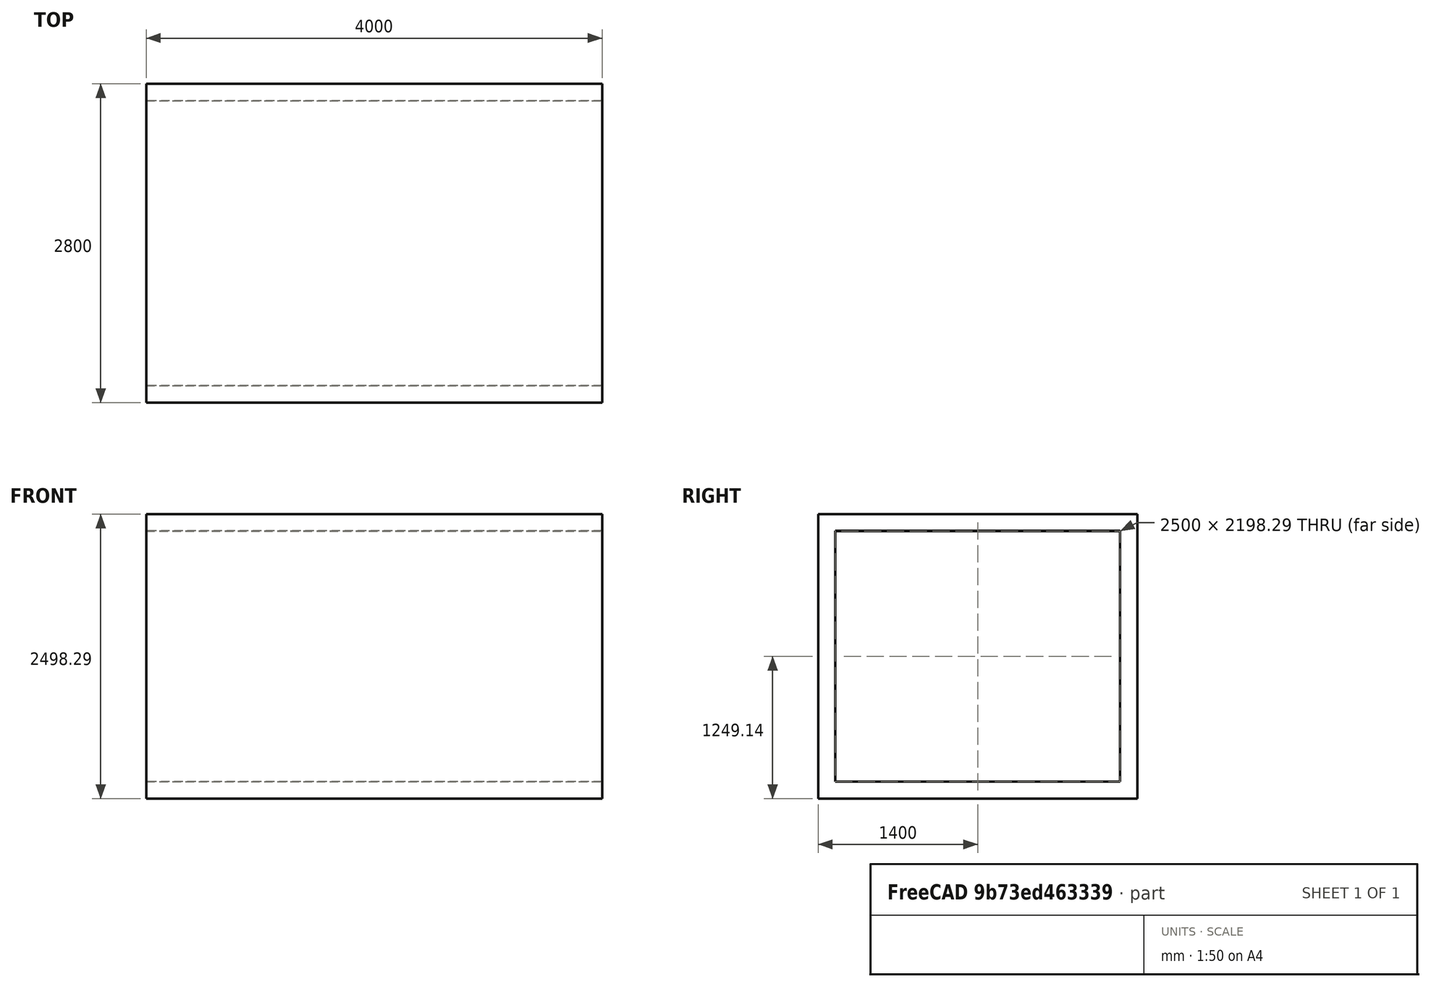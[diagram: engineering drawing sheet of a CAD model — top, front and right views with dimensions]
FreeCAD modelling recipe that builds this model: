
FCSTD DOCUMENT  (FreeCAD 0.17R10276 (Git))
Label: Model 01
License: CreativeCommons Attribution
LicenseURL: http://creativecommons.org/licenses/by/4.0/
objects: Part::Feature×203, Part::Part2DObjectPython×172, App::FeaturePython×39, Part::Mirroring×20, App::DocumentObjectGroup×15, App::Annotation×12, Part::Compound×9, Part::Extrusion×2, Part::FeaturePython×2, Part::Thickness×1, Sketcher::SketchObject×1
note: 410 computed .brp shape members not serialized (recipe doc carries the construction recipe); baked Part::Feature solids carry a one-line shape summary decoded from their .brp

FEATURE [Part::Part2DObjectPython] Rectangle  # Draft 2D object (typed FeaturePython)
  ChamferSize = 0
  Columns = 1
  FilletRadius = 0
  Height = 7500
  Length = 6000
  MakeFace = false
  MapMode = -1
  Placement = pos=(-92,-160,0) rot=(0,0,1;0rad)
  Rows = 1
FEATURE [App::FeaturePython] Dimension  # Draft dimension (typed FeaturePython)
  Diameter = false
  Dimline = (6612,4842,0)
  Direction = (0,0,0)
  Distance = 7500
  End = (5908,7340,0)
  LinkedGeometry = -> [Rectangle]
  Normal = (0,0,1)
  Start = (5908,-160,0)
  Support = -> Rectangle
FEATURE [App::FeaturePython] Dimension001  # Draft dimension (typed FeaturePython)
  Diameter = false
  Dimline = (3172,-852,0)
  Direction = (0,0,0)
  Distance = 6000
  End = (5908,-160,0)
  LinkedGeometry = -> [Rectangle]
  Normal = (0,0,1)
  Start = (-92,-160,0)
  Support = -> Rectangle
FEATURE [Part::Part2DObjectPython] Rectangle001  # Draft 2D object (typed FeaturePython)
  ChamferSize = 0
  Columns = 1
  FilletRadius = 0
  Height = 9000
  Length = 5000
  MakeFace = false
  MapMode = -1
  Placement = pos=(9194.87,-160,0) rot=(0,0,1;0rad)
  Rows = 1
FEATURE [App::FeaturePython] Dimension002  # Draft dimension (typed FeaturePython)
  Diameter = false
  Dimline = (15053,4856,0)
  Direction = (0,0,0)
  Distance = 9000
  End = (14194.9,8840,0)
  LinkedGeometry = -> [Rectangle001]
  Normal = (0,0,1)
  Start = (14194.9,-160,0)
  Support = -> Rectangle001
FEATURE [App::FeaturePython] Dimension003  # Draft dimension (typed FeaturePython)
  Diameter = false
  Dimline = (12458.9,-852,0)
  Direction = (0,0,0)
  Distance = 5000
  End = (14194.9,-160,0)
  LinkedGeometry = -> [Rectangle001]
  Normal = (0,0,1)
  Start = (9194.87,-160,0)
  Support = -> Rectangle001
FEATURE [Part::Part2DObjectPython] Rectangle002  # Draft 2D object (typed FeaturePython)
  ChamferSize = 0
  Columns = 1
  FilletRadius = 0
  Height = 11250
  Length = 4000
  MakeFace = false
  MapMode = -1
  Placement = pos=(17670.3,-160,0) rot=(0,0,1;0rad)
  Rows = 1
FEATURE [App::FeaturePython] Dimension004  # Draft dimension (typed FeaturePython)
  Diameter = false
  Dimline = (22786,4857,0)
  Direction = (0,0,0)
  Distance = 11250
  End = (21670.3,11090,0)
  LinkedGeometry = -> [Rectangle002]
  Normal = (0,0,1)
  Start = (21670.3,-160,0)
  Support = -> Rectangle002
FEATURE [App::FeaturePython] Dimension005  # Draft dimension (typed FeaturePython)
  Diameter = false
  Dimline = (20934.3,-852,0)
  Direction = (0,0,0)
  Distance = 4000
  End = (21670.3,-160,0)
  LinkedGeometry = -> [Rectangle002]
  Normal = (0,0,1)
  Start = (17670.3,-160,0)
  Support = -> Rectangle002
FEATURE [Part::Part2DObjectPython] Rectangle011  # Draft 2D object (typed FeaturePython)
  ChamferSize = 0
  Columns = 1
  FilletRadius = 0
  Height = 18
  Length = 900
  MakeFace = true
  Placement = pos=(3354.54,473.858,0) rot=(0.707107,0.707107,0;3.14159rad)
  Rows = 1
FEATURE [Part::Part2DObjectPython] Arc001  # Draft 2D object (typed FeaturePython)
  FirstAngle = -90
  LastAngle = 0
  MakeFace = true
  Placement = pos=(3372.54,473.858,0) rot=(0.707107,0.707107,0;3.14159rad)
  Radius = 900
FEATURE [Part::Part2DObjectPython] Rectangle012  # Draft 2D object (typed FeaturePython)
  ChamferSize = 0
  Columns = 1
  FilletRadius = 0
  Height = 18
  Length = 100
  MakeFace = true
  Placement = pos=(3390.54,373.858,0) rot=(0.707107,0.707107,0;3.14159rad)
  Rows = 1
FEATURE [Part::Part2DObjectPython] Rectangle013  # Draft 2D object (typed FeaturePython)
  ChamferSize = 0
  Columns = 1
  FilletRadius = 0
  Height = 18
  Length = 100
  MakeFace = true
  Placement = pos=(3372.54,373.858,0) rot=(0.707107,0.707107,0;3.14159rad)
  Rows = 1
FEATURE [Part::Part2DObjectPython] Rectangle014  # Draft 2D object (typed FeaturePython)
  ChamferSize = 0
  Columns = 1
  FilletRadius = 0
  Height = 18
  Length = 100
  MakeFace = true
  Placement = pos=(2436.54,373.858,0) rot=(0.707107,0.707107,0;3.14159rad)
  Rows = 1
FEATURE [Part::Part2DObjectPython] Rectangle015  # Draft 2D object (typed FeaturePython)
  ChamferSize = 0
  Columns = 1
  FilletRadius = 0
  Height = 18
  Length = 100
  MakeFace = true
  Placement = pos=(2454.54,373.858,0) rot=(0.707107,0.707107,0;3.14159rad)
  Rows = 1
FEATURE [Part::Compound] Compound001  label="Door-90cm"
  Links = -> [Rectangle015,Rectangle014,Rectangle011,Rectangle012,Arc001,Rectangle013]
  Placement = pos=(12065.1,-4816.3,0) rot=(0,0,1;0rad)
FEATURE [Part::Part2DObjectPython] Rectangle016  # Draft 2D object (typed FeaturePython)
  ChamferSize = 0
  Columns = 1
  FilletRadius = 0
  Height = 1450
  Length = 2250
  MakeFace = false
  Placement = pos=(19234,-3969.83,0) rot=(0.707107,0.707107,0;3.14159rad)
  Rows = 1
FEATURE [Part::Part2DObjectPython] Rectangle017  # Draft 2D object (typed FeaturePython)
  ChamferSize = 0
  Columns = 1
  FilletRadius = 0
  Height = 18
  Length = 800
  MakeFace = true
  Placement = pos=(4414.52,473.858,0) rot=(0.707107,0.707107,0;3.14159rad)
  Rows = 1
FEATURE [Part::Part2DObjectPython] Rectangle018  # Draft 2D object (typed FeaturePython)
  ChamferSize = 0
  Columns = 1
  FilletRadius = 0
  Height = 18
  Length = 100
  MakeFace = true
  Placement = pos=(4450.52,373.858,0) rot=(0.707107,0.707107,0;3.14159rad)
  Rows = 1
FEATURE [Part::Part2DObjectPython] Rectangle019  # Draft 2D object (typed FeaturePython)
  ChamferSize = 0
  Columns = 1
  FilletRadius = 0
  Height = 18
  Length = 100
  MakeFace = true
  Placement = pos=(4432.52,373.858,0) rot=(0.707107,0.707107,0;3.14159rad)
  Rows = 1
FEATURE [Part::Part2DObjectPython] Rectangle020  # Draft 2D object (typed FeaturePython)
  ChamferSize = 0
  Columns = 1
  FilletRadius = 0
  Height = 18
  Length = 100
  MakeFace = true
  Placement = pos=(3596.52,373.858,0) rot=(0.707107,0.707107,0;3.14159rad)
  Rows = 1
FEATURE [Part::Part2DObjectPython] Rectangle021  # Draft 2D object (typed FeaturePython)
  ChamferSize = 0
  Columns = 1
  FilletRadius = 0
  Height = 18
  Length = 100
  MakeFace = true
  Placement = pos=(3614.52,373.858,0) rot=(0.707107,0.707107,0;3.14159rad)
  Rows = 1
FEATURE [Part::Part2DObjectPython] Rectangle022  # Draft 2D object (typed FeaturePython)
  ChamferSize = 0
  Columns = 1
  FilletRadius = 0
  Height = 1655.27
  Length = 2455.27
  MakeFace = false
  Placement = pos=(19131.4,-4072.46,0) rot=(0.707107,0.707107,0;3.14159rad)
  Rows = 1
FEATURE [Part::Part2DObjectPython] Rectangle023  # Draft 2D object (typed FeaturePython)
  ChamferSize = 0
  Columns = 1
  FilletRadius = 0
  Height = 800
  Length = 800
  MakeFace = true
  Placement = pos=(21405.4,-1242.94,0) rot=(0.707107,0.707107,0;3.14159rad)
  Rows = 1
FEATURE [Part::Part2DObjectPython] Rectangle024  # Draft 2D object (typed FeaturePython)
  ChamferSize = 0
  Columns = 1
  FilletRadius = 0
  Height = 760
  Length = 760
  MakeFace = true
  Placement = pos=(21425.4,-1222.94,0) rot=(0.707107,0.707107,0;3.14159rad)
  Rows = 1
FEATURE [Part::Feature] Face
  Placement = pos=(15980.4,-1398.57,0) rot=(0,0,1;0rad)
  shape: bbox 800 x 800 x 2e-07 mm, 1 faces, 0 solids (baked)
FEATURE [Part::Part2DObjectPython] Rectangle025  # Draft 2D object (typed FeaturePython)
  ChamferSize = 0
  Columns = 1
  FilletRadius = 0
  Height = 760
  Length = 760
  MakeFace = true
  Placement = pos=(21425.4,-1222.94,0) rot=(0.707107,0.707107,0;3.14159rad)
  Rows = 1
FEATURE [Part::Part2DObjectPython] Line001  # Draft 2D object (typed FeaturePython)
  ChamferSize = 0
  Closed = false
  End = (21425.4,-1222.94,0)
  FilletRadius = 0
  Length = 1074.8
  MakeFace = true
  Placement = pos=(15980.4,-1398.57,0) rot=(0,0,1;0rad)
  Points = (2) [(6204.98,935.631,0),(5444.98,175.631,0)]
  Start = (22185.4,-462.938,0)
  Subdivisions = 0
FEATURE [Part::Part2DObjectPython] Line002  # Draft 2D object (typed FeaturePython)
  ChamferSize = 0
  Closed = false
  End = (22185.4,-1222.94,0)
  FilletRadius = 0
  Length = 1074.8
  MakeFace = true
  Placement = pos=(15980.4,-1398.57,0) rot=(0,0,1;0rad)
  Points = (2) [(5444.98,935.631,0),(6204.98,175.631,0)]
  Start = (21425.4,-462.938,0)
  Subdivisions = 0
FEATURE [Part::Part2DObjectPython] Block  label="Shower"  # Draft 2D object (typed FeaturePython)
  Components = -> [Line002,Line001,Rectangle025,Face]
  Placement = pos=(-1521.4,-1276.89,0) rot=(0,0,1;0rad)
FEATURE [Part::Part2DObjectPython] Rectangle026  # Draft 2D object (typed FeaturePython)
  ChamferSize = 0
  Columns = 1
  FilletRadius = 30
  Height = 370
  Length = 170
  MakeFace = true
  Placement = pos=(22375.3,-1817.54,0) rot=(0.707107,0.707107,0;3.14159rad)
  Rows = 1
FEATURE [Part::Part2DObjectPython] Circle  # Draft 2D object (typed FeaturePython)
  FirstAngle = 0
  LastAngle = 0
  MakeFace = true
  Placement = pos=(22560.3,-1732.54,0) rot=(0.707107,0.707107,0;3.14159rad)
  Radius = 10
  Support = -> [Rectangle026]
FEATURE [Part::Feature] Compound003  label="WC001"
  Placement = pos=(12977.9,-1470.8,0) rot=(0,0,1;0rad)
  shape: bbox 370 x 660 x 2e-07 mm, 2 faces, 0 solids (baked)
FEATURE [Part::Part2DObjectPython] Rectangle027  # Draft 2D object (typed FeaturePython)
  ChamferSize = 0
  Columns = 1
  FilletRadius = 50
  Height = 300
  Length = 500
  MakeFace = true
  Placement = pos=(21444.9,-2450.78,0) rot=(0.707107,0.707107,0;3.14159rad)
  Rows = 1
FEATURE [Part::Part2DObjectPython] Circle001  # Draft 2D object (typed FeaturePython)
  FirstAngle = 0
  LastAngle = 0
  MakeFace = true
  Placement = pos=(5532.19,-802.214,0) rot=(0,0,1;0rad)
  Radius = 12
FEATURE [Part::Feature] Face003
  shape: bbox 278.9 x 478.9 x 2e-07 mm, 1 faces, 0 solids (baked)
FEATURE [Part::Feature] Face004
  Placement = pos=(15980.4,-1398.57,0) rot=(0,0,1;0rad)
  shape: bbox 278.9 x 478.9 x 2e-07 mm, 1 faces, 0 solids (baked)
FEATURE [Part::Feature] Face005
  shape: bbox 300 x 500 x 2e-07 mm, 1 faces, 0 solids (baked)
FEATURE [Part::Compound] Compound004  label="Sink 1"
  Links = -> [Face005,Face003,Circle001]
  Placement = pos=(13769.5,-2367.61,0) rot=(0,0,1;0rad)
FEATURE [Part::Feature] Compound005  label="Sink"
  Placement = pos=(18979.2,3570.08,0) rot=(0,0,-1;1.5708rad)
  shape: bbox 500 x 300 x 2e-07 mm, 3 faces, 0 solids (baked)
FEATURE [Part::Feature] Compound006  label="WC002"
  Placement = pos=(12181.7,-1602.71,0) rot=(0,0,1;0rad)
  shape: bbox 370 x 660 x 2e-07 mm, 2 faces, 0 solids (baked)
FEATURE [Part::Part2DObjectPython] Arc002  # Draft 2D object (typed FeaturePython)
  FirstAngle = -90
  LastAngle = 0
  MakeFace = true
  Placement = pos=(4432.52,473.858,0) rot=(0.707107,0.707107,0;3.14159rad)
  Radius = 800
FEATURE [Part::Compound] Compound007  label="Door-80cm"
  Links = -> [Rectangle019,Rectangle017,Rectangle018,Rectangle020,Rectangle021,Arc002]
  Placement = pos=(12065.1,-4816.3,0) rot=(0,0,1;0rad)
FEATURE [Part::Part2DObjectPython] Rectangle028  # Draft 2D object (typed FeaturePython)
  ChamferSize = 0
  Columns = 1
  FilletRadius = 0
  Height = 400
  Length = 400
  MakeFace = true
  Placement = pos=(17670.3,-160,0) rot=(0.707107,0.707107,0;3.14159rad)
  Rows = 1
  Support = -> [Rectangle002]
FEATURE [Part::Feature] mirror008  label="Mirror of 90cm door001"
  Placement = pos=(3560.22,2517.25,0) rot=(0,0,1;0rad)
  shape: bbox 972 x 1000 x 2e-07 mm, 5 faces, 0 solids (baked)
FEATURE [Part::Feature] Compound010  label="90cm door003"
  Placement = pos=(22653.3,641.465,0) rot=(0,0,1;0rad)
  shape: bbox 972 x 1000 x 2e-07 mm, 5 faces, 0 solids (baked)
FEATURE [Part::Part2DObjectPython] Line003  # Draft 2D object (typed FeaturePython)
  ChamferSize = 0
  Closed = false
  End = (23811.8,1115.32,0)
  FilletRadius = 0
  Length = 1314
  MakeFace = true
  Placement = pos=(4391.51,-222,0) rot=(0,0,1;0rad)
  Points = (2) [(20734.3,1337.32,0),(19420.3,1337.32,0)]
  Start = (25125.8,1115.32,0)
  Subdivisions = 0
FEATURE [Part::Part2DObjectPython] Line  # Draft 2D object (typed FeaturePython)
  ChamferSize = 0
  Closed = false
  End = (26367.1,1115.32,0)
  FilletRadius = 0
  Length = 2499.64
  MakeFace = true
  Placement = pos=(4497.18,0,0) rot=(0,0,1;0rad)
  Points = (2) [(19370.3,1115.32,0),(21870,1115.32,0)]
  Start = (23867.5,1115.32,0)
  Subdivisions = 0
FEATURE [Part::Part2DObjectPython] Line005  # Draft 2D object (typed FeaturePython)
  ChamferSize = 0
  Closed = false
  End = (26261.5,960.561,0)
  FilletRadius = 0
  Length = 2499.64
  MakeFace = true
  Placement = pos=(4391.51,0,0) rot=(0,0,1;0rad)
  Points = (2) [(19370.3,960.561,0),(21870,960.561,0)]
  Start = (23761.8,960.561,0)
  Subdivisions = 0
FEATURE [App::DocumentObjectGroup] Construction
  Group = -> [Compound010,Line003,Line,Line005]
FEATURE [Part::Part2DObjectPython] Rectangle049  # Draft 2D object (typed FeaturePython)
  ChamferSize = 0
  Columns = 1
  FilletRadius = 0
  Height = 1900
  Length = 1400
  MakeFace = true
  Placement = pos=(-5091.08,-778.605,0) rot=(0,0,1;0rad)
  Rows = 1
FEATURE [Part::Part2DObjectPython] Rectangle050  # Draft 2D object (typed FeaturePython)
  ChamferSize = 0
  Columns = 1
  FilletRadius = 0
  Height = 1900
  Length = 910
  MakeFace = true
  Placement = pos=(-6241.3,-778.605,0) rot=(0,0,1;0rad)
  Rows = 1
FEATURE [Part::Part2DObjectPython] Rectangle051  # Draft 2D object (typed FeaturePython)
  ChamferSize = 0
  Columns = 1
  FilletRadius = 0
  Height = 300
  Length = 910
  MakeFace = true
  Placement = pos=(-6241.3,821.395,0) rot=(0,0,1;0rad)
  Rows = 1
FEATURE [Part::Part2DObjectPython] Line008  # Draft 2D object (typed FeaturePython)
  ChamferSize = 0
  Closed = false
  End = (-5786.3,821.395,0)
  FilletRadius = 0
  Length = 647.012
  MakeFace = true
  Points = (2) [(-6241.3,361.395,0),(-5786.3,821.395,0)]
  Start = (-6241.3,361.395,0)
  Subdivisions = 0
FEATURE [Part::Part2DObjectPython] DWire001  # Draft 2D object (typed FeaturePython)
  ChamferSize = 0
  Closed = true
  End = (-6241.3,361.395,0)
  FilletRadius = 0
  Length = 1562.01
  MakeFace = true
  Points = (3) [(-5786.3,821.395,0),(-5786.3,361.395,0),(-6241.3,361.395,0)]
  Start = (-5786.3,821.395,0)
  Subdivisions = 0
FEATURE [Part::Part2DObjectPython] DWire002  # Draft 2D object (typed FeaturePython)
  ChamferSize = 0
  Closed = true
  End = (-5091.08,361.395,0)
  FilletRadius = 0
  Length = 1562.01
  MakeFace = true
  Placement = pos=(1150.22,0,0) rot=(0,0,1;0rad)
  Points = (3) [(-5786.3,821.395,0),(-5786.3,361.395,0),(-6241.3,361.395,0)]
  Start = (-4636.08,821.395,0)
  Subdivisions = 0
FEATURE [Part::Part2DObjectPython] Rectangle052  # Draft 2D object (typed FeaturePython)
  ChamferSize = 0
  Columns = 1
  FilletRadius = 0
  Height = 300
  Length = 700
  MakeFace = true
  Placement = pos=(-5091.08,821.395,0) rot=(0,0,1;0rad)
  Rows = 1
FEATURE [Part::Part2DObjectPython] Rectangle053  # Draft 2D object (typed FeaturePython)
  ChamferSize = 0
  Columns = 1
  FilletRadius = 0
  Height = 300
  Length = 700
  MakeFace = true
  Placement = pos=(-4391.08,821.395,0) rot=(0,0,1;0rad)
  Rows = 1
FEATURE [Part::Compound] Compound009  label="Bed-Twin"
  Links = -> [Rectangle050,Rectangle051,Line008,DWire001]
FEATURE [App::DocumentObjectGroup] Group003  label="Assets"
  Group = -> [Compound005,Compound006,Compound001,Compound007,Compound009]
FEATURE [Part::Part2DObjectPython] DWire005  # Draft 2D object (typed FeaturePython)
  ChamferSize = 0
  Closed = true
  End = (-3474.44,-2441.09,0)
  FilletRadius = 0
  Length = 5366.71
  MakeFace = true
  Points = (8) [(-3691.08,-2441.09,0),(-3691.08,-1691.09,0),(-2291.08,-1691.09,0),(-2291.08,-2441.09,0),(-2507.72,-2441.09,0),(-2507.72,-1907.73,0),+2 more]
  Start = (-3691.08,-2441.09,0)
  Subdivisions = 0
FEATURE [Part::Part2DObjectPython] Rectangle035  # Draft 2D object (typed FeaturePython)
  ChamferSize = 0
  Columns = 1
  FilletRadius = 0
  Height = 533.356
  Length = 966.713
  MakeFace = true
  Placement = pos=(-3474.44,-2441.09,0) rot=(0,0,1;0rad)
  Rows = 1
FEATURE [Part::Part2DObjectPython] Line012  # Draft 2D object (typed FeaturePython)
  ChamferSize = 0
  Closed = false
  End = (-2991.08,-2441.09,0)
  FilletRadius = 0
  Length = 533.356
  MakeFace = true
  Points = (2) [(-2991.08,-1907.73,0),(-2991.08,-2441.09,0)]
  Start = (-2991.08,-1907.73,0)
  Subdivisions = 0
FEATURE [Part::Part2DObjectPython] Line004  # Draft 2D object (typed FeaturePython)
  ChamferSize = 0
  Closed = false
  End = (-947.957,-2441.09,0)
  FilletRadius = 0
  Length = 533.356
  MakeFace = true
  Placement = pos=(2043.12,0,0) rot=(0,0,1;0rad)
  Points = (2) [(-2991.08,-1907.73,0),(-2991.08,-2441.09,0)]
  Start = (-947.957,-1907.73,0)
  Subdivisions = 0
FEATURE [Part::Part2DObjectPython] DWire006  # Draft 2D object (typed FeaturePython)
  ChamferSize = 0
  Closed = true
  End = (-1431.31,-2441.09,0)
  FilletRadius = 0
  Length = 6333.43
  MakeFace = true
  Placement = pos=(2043.12,0,0) rot=(0,0,1;0rad)
  Points = (8) [(-3691.08,-2441.09,0),(-3691.08,-1691.09,0),(-1807.72,-1691.09,0),(-1807.72,-2441.09,0),(-2024.37,-2441.09,0),(-2024.37,-1907.73,0),+2 more]
  Start = (-1647.96,-2441.09,0)
  Subdivisions = 0
FEATURE [Part::Part2DObjectPython] DWire007  # Draft 2D object (typed FeaturePython)
  ChamferSize = 0
  Closed = true
  End = (-5457.85,-2441.09,0)
  FilletRadius = 0
  Length = 4400
  MakeFace = true
  Placement = pos=(-1983.42,0,0) rot=(0,0,1;0rad)
  Points = (8) [(-3691.08,-2441.09,0),(-3691.08,-1691.09,0),(-2774.44,-1691.09,0),(-2774.44,-2441.09,0),(-2991.08,-2441.09,0),(-2991.08,-1907.73,0),+2 more]
  Start = (-5674.49,-2441.09,0)
  Subdivisions = 0
FEATURE [Part::Part2DObjectPython] Rectangle037  # Draft 2D object (typed FeaturePython)
  ChamferSize = 0
  Columns = 1
  FilletRadius = 0
  Height = 533.356
  Length = 483.356
  MakeFace = true
  Placement = pos=(-5457.85,-2441.09,0) rot=(0,0,1;0rad)
  Rows = 1
FEATURE [Part::Compound] Compound021  label="Sofa - 1"
  Links = -> [DWire005,Rectangle035,Line012]
FEATURE [Part::Compound] Compound011  label="Sofa - 2"
  Links = -> [Rectangle037,DWire007]
FEATURE [Part::Part2DObjectPython] Rectangle038  # Draft 2D object (typed FeaturePython)
  ChamferSize = 0
  Columns = 1
  FilletRadius = 0
  Height = 533.356
  Length = 1450.07
  MakeFace = true
  Placement = pos=(-1431.31,-2441.09,0) rot=(0,0,1;0rad)
  Rows = 1
FEATURE [Part::Part2DObjectPython] Line006  # Draft 2D object (typed FeaturePython)
  ChamferSize = 0
  Closed = false
  End = (-464.6,-2441.09,0)
  FilletRadius = 0
  Length = 533.356
  MakeFace = true
  Placement = pos=(2526.48,0,0) rot=(0,0,1;0rad)
  Points = (2) [(-2991.08,-1907.73,0),(-2991.08,-2441.09,0)]
  Start = (-464.6,-1907.73,0)
  Subdivisions = 0
FEATURE [Part::Compound] Compound022  label="Sofa - 3"
  Links = -> [Line004,DWire006,Rectangle038,Line006]
FEATURE [Part::Compound] Compound008  label="Bed-Double"
  Links = -> [Rectangle049,DWire002,Rectangle052,Rectangle053]
FEATURE [Part::Feature] Compound024  label="90cm door005"
  Placement = pos=(26285.8,79.011,0) rot=(0,0,1;1.5708rad)
  shape: bbox 1000 x 972 x 2e-07 mm, 5 faces, 0 solids (baked)
FEATURE [Part::Part2DObjectPython] Rectangle054  # Draft 2D object (typed FeaturePython)
  ChamferSize = 0
  Columns = 1
  FilletRadius = 0
  Height = 600
  Length = 2923.45
  MakeFace = true
  Placement = pos=(18270.3,2237.32,0) rot=(0,0,1;1.5708rad)
  Rows = 1
FEATURE [Part::Mirroring] mirror009  label="Mirror of Sink"
  Base = (18377,-1894.45,0)
  Normal = (0,1,0)
  Source = -> Compound005
FEATURE [Part::Feature] mirror010  label="Mirror of Sink001"
  Placement = pos=(19714.8,21927.3,0) rot=(0,0,-1;1.5708rad)
  shape: bbox 300 x 500 x 2e-07 mm, 3 faces, 0 solids (baked)
FEATURE [Part::Feature] Shell002  label="Dinning 002"
  Placement = pos=(-2420.47,1941.18,0) rot=(0,0,1;0rad)
  shape: bbox 2057 x 2057 x 2e-07 mm, 5 faces, 0 solids (baked)
FEATURE [Part::Feature] Shell003  label="Dinning 003"
  Placement = pos=(-7725.86,-2470.88,0) rot=(0,0,1;0rad)
  shape: bbox 2057 x 2057 x 2e-07 mm, 5 faces, 0 solids (baked)
FEATURE [Part::Feature] Compound027  label="dinning001"
  Placement = pos=(-14334.8,-3411.08,0) rot=(0,0,1;0rad)
  shape: bbox 2057 x 1200 x 2e-07 mm, 5 faces, 0 solids (baked)
FEATURE [Part::Feature] Compound030  label="Bed-Double003"
  Placement = pos=(9599.08,5590.61,0) rot=(0,0,1;0rad)
  shape: bbox 1400 x 1900 x 2e-07 mm, 4 faces, 0 solids (baked)
FEATURE [Part::Feature] mirror013  label="Mirror of Shower002"
  Placement = pos=(-9357.23,5973.34,0) rot=(0,0,1;0rad)
  shape: bbox 800 x 800 x 2e-07 mm, 2 faces, 0 solids (baked)
FEATURE [Part::Feature] mirror017  label="Mirror of Sofa - 006"
  Placement = pos=(5211.98,2057.23,0) rot=(0,0,1;0rad)
  shape: bbox 1400 x 750 x 2e-07 mm, 2 faces, 0 solids (baked)
FEATURE [Part::Feature] Compound031  label="Sofa - 006"
  Placement = pos=(27672.7,9569.4,0) rot=(0,0,1;0rad)
  shape: bbox 1400 x 750 x 2e-07 mm, 2 faces, 0 solids (baked)
FEATURE [Part::Feature] Compound034  label="Bed-Double004"
  Placement = pos=(15177.5,-4723.55,0) rot=(0,0,1;0rad)
  shape: bbox 1400 x 1900 x 2e-07 mm, 4 faces, 0 solids (baked)
FEATURE [Part::Feature] Compound035  label="Bed-Double005"
  Placement = pos=(12639.4,2140.46,0) rot=(0,0,1;1.5708rad)
  shape: bbox 1900 x 1400 x 2e-07 mm, 4 faces, 0 solids (baked)
FEATURE [Part::Part2DObjectPython] Rectangle070  # Draft 2D object (typed FeaturePython)
  ChamferSize = 0
  Columns = 1
  FilletRadius = 0
  Height = 3000
  Length = 3000
  MakeFace = true
  Placement = pos=(6000,-9774.06,0) rot=(0,0,1;0rad)
  Rows = 1
FEATURE [Part::Part2DObjectPython] Rectangle072  # Draft 2D object (typed FeaturePython)
  ChamferSize = 0
  Columns = 1
  FilletRadius = 0
  Height = 600
  Length = 3599.13
  MakeFace = true
  Placement = pos=(2308.87,8523.32,0) rot=(0,0,1;0rad)
  Rows = 1
FEATURE [Part::Feature] mirror030  label="Mirror of Sink 005"
  Placement = pos=(4044.83,28204.3,0) rot=(0,0,-1;1.5708rad)
  shape: bbox 500 x 300 x 2e-07 mm, 3 faces, 0 solids (baked)
FEATURE [Part::Part2DObjectPython] Rectangle073  # Draft 2D object (typed FeaturePython)
  ChamferSize = 0
  Columns = 1
  FilletRadius = 0
  Height = 1950
  Length = 950
  MakeFace = true
  Placement = pos=(1798.43,-5839.95,0) rot=(0,0,1;0rad)
  Rows = 1
FEATURE [App::DocumentObjectGroup] Group006  label="Plan Layout 2"
  Group = -> [Compound035,Rectangle070,Rectangle073]
FEATURE [App::DocumentObjectGroup] Group001  label="9mx5m"
  Group = -> [Dimension002,Dimension003,Rectangle001,Group006]
FEATURE [Part::Feature] Compound048
  Placement = pos=(2515.93,6885.08,0) rot=(0,0,-1;1.5708rad)
  shape: bbox 1950 x 2057 x 2e-07 mm, 7 faces, 0 solids (baked)
FEATURE [Part::Feature] Compound049
  Placement = pos=(-6428.78,862.396,0) rot=(0,0,1;0rad)
  shape: bbox 2057 x 1950 x 2e-07 mm, 7 faces, 0 solids (baked)
FEATURE [Part::Part2DObjectPython] Line016  # Draft 2D object (typed FeaturePython)
  ChamferSize = 0
  Closed = false
  End = (5908,8823.32,0)
  FilletRadius = 0
  Length = 3599.13
  MakeFace = true
  Placement = pos=(0,1783.32,0) rot=(0,0,1;0rad)
  Points = (2) [(2308.87,7040,0),(5908,7040,0)]
  Start = (2308.87,8823.32,0)
  Subdivisions = 0
FEATURE [Part::Part2DObjectPython] Rectangle075  # Draft 2D object (typed FeaturePython)
  ChamferSize = 0
  Columns = 1
  FilletRadius = 0
  Height = 600
  Length = 150.814
  MakeFace = false
  Placement = pos=(3257.19,2489.19,0) rot=(0,0,1;0rad)
  Rows = 1
FEATURE [Part::Part2DObjectPython] Rectangle078  # Draft 2D object (typed FeaturePython)
  ChamferSize = 0
  Columns = 1
  FilletRadius = 0
  Height = 2500
  Length = 4000
  MakeFace = false
  Placement = pos=(17670.3,8590,0) rot=(0,0,1;0rad)
  Rows = 1
FEATURE [Part::Part2DObjectPython] Rectangle079  # Draft 2D object (typed FeaturePython)
  ChamferSize = 0
  Columns = 1
  FilletRadius = 0
  Height = 7500
  Length = 3752.68
  MakeFace = false
  Placement = pos=(2155.32,-160,0) rot=(0,0,1;0rad)
  Rows = 7
FEATURE [App::Annotation] Text
  LabelText = Single Bed Unit 45 sq m | 1 Bed | Bath | Kitchen | Living
  Position = (-173.725,11590.6,0)
FEATURE [Part::Part2DObjectPython] Line017  # Draft 2D object (typed FeaturePython)
  ChamferSize = 0
  Closed = false
  End = (19420.3,11090,0)
  FilletRadius = 0
  Length = 8852.68
  MakeFace = true
  Points = (2) [(19420.3,2237.32,0),(19420.3,11090,0)]
  Start = (19420.3,2237.32,0)
  Subdivisions = 0
FEATURE [Part::Feature] Compound012  label="Bed-Double002"
  Placement = pos=(18791.7,14231.1,0) rot=(0,0,1;1.5708rad)
  shape: bbox 1900 x 1400 x 2e-07 mm, 4 faces, 0 solids (baked)
FEATURE [App::DocumentObjectGroup] Group005  label="Plan Layout 3"
  Group = -> [Rectangle054,Compound012,mirror017,Compound031,Compound024,mirror010]
FEATURE [App::DocumentObjectGroup] Group002  label="11.5mx4m"
  Group = -> [Dimension004,Dimension005,Rectangle002,Group005]
FEATURE [Part::Feature] Compound  label="Sofa - 007"
  Placement = pos=(19318.3,10129.4,0) rot=(0,0,1;0rad)
  shape: bbox 1883 x 750 x 2e-07 mm, 2 faces, 0 solids (baked)
FEATURE [Part::Part2DObjectPython] Rectangle082  # Draft 2D object (typed FeaturePython)
  ChamferSize = 0
  Columns = 1
  FilletRadius = 0
  Height = 2803.44
  Length = 4303.44
  MakeFace = false
  Placement = pos=(17518.6,8438.28,0) rot=(0,0,1;0rad)
  Rows = 1
FEATURE [App::DocumentObjectGroup] Group007  label="Info"
  Group = -> [Text]
FEATURE [Part::Part2DObjectPython] Rectangle083  # Draft 2D object (typed FeaturePython)
  ChamferSize = 0
  Columns = 1
  FilletRadius = 0
  Height = 950
  Length = 950
  MakeFace = true
  Placement = pos=(18152.7,6324.53,0) rot=(0.707107,0.707107,0;3.14159rad)
  Rows = 1
FEATURE [Part::Feature] mirror035  label="Mirror of Sofa - 016"
  shape: bbox 1883 x 750 x 2e-07 mm, 2 faces, 0 solids (baked)
FEATURE [Part::Part2DObjectPython] Line023  # Draft 2D object (typed FeaturePython)
  ChamferSize = 0
  Closed = false
  End = (21670.3,5160.77,0)
  FilletRadius = 0
  Length = 4000
  MakeFace = true
  Points = (2) [(17670.3,5160.77,0),(21670.3,5160.77,0)]
  Start = (17670.3,5160.77,0)
  Subdivisions = 0
FEATURE [Part::Feature] Compound051  label="dinning003"
  Placement = pos=(29919.6,-14497.4,0) rot=(0,0,1;1.5708rad)
  shape: bbox 1200 x 2057 x 2e-07 mm, 5 faces, 0 solids (baked)
FEATURE [Part::Part2DObjectPython] Rectangle090  # Draft 2D object (typed FeaturePython)
  ChamferSize = 0
  Columns = 1
  FilletRadius = 0
  Height = 3349.19
  Length = 150
  MakeFace = false
  Placement = pos=(-92,1289.19,0) rot=(0,0,-1;1.5708rad)
  Rows = 1
FEATURE [Part::Feature] mirror044  label="Mirror of Mirror of Shower002"
  Placement = pos=(-2698.48,-4e-12,0) rot=(0,0,1;0rad)
  shape: bbox 800 x 800 x 2e-07 mm, 2 faces, 0 solids (baked)
FEATURE [Part::Feature] mirror045  label="Mirror of Mirror of WC003"
  Placement = pos=(-2698.48,-4e-12,0) rot=(0,0,1;0rad)
  shape: bbox 370 x 660 x 2e-07 mm, 2 faces, 0 solids (baked)
FEATURE [Part::Feature] mirror046  label="Mirror of Rectangle090"
  Placement = pos=(-2698.48,-4e-12,0) rot=(0,0,1;0rad)
  shape: bbox 1900 x 2547 x 2e-07 mm, 0 faces, 0 solids (baked)
FEATURE [Part::Feature] mirror047  label="Mirror of Rectangle091"
  Placement = pos=(-2698.48,-4e-12,0) rot=(0,0,1;0rad)
  shape: bbox 1600 x 2247 x 2e-07 mm, 0 faces, 0 solids (baked)
FEATURE [Part::Feature] mirror048  label="Mirror of Mirror of Sink 007"
  Placement = pos=(-2698.48,-4e-12,0) rot=(0,0,1;0rad)
  shape: bbox 300 x 500 x 2e-07 mm, 3 faces, 0 solids (baked)
FEATURE [Part::Part2DObjectPython] Rectangle092  # Draft 2D object (typed FeaturePython)
  ChamferSize = 0
  Columns = 6
  FilletRadius = 0
  Height = 4000
  Length = 6502.68
  MakeFace = false
  Placement = pos=(17670.3,2087.32,0) rot=(0.707107,0.707107,0;3.14159rad)
  Rows = 1
FEATURE [Part::Feature] Compound052  label="Sofa - 008"
  Placement = pos=(1555.96,6630.22,0) rot=(0,0,1;0rad)
  shape: bbox 1883 x 750 x 2e-07 mm, 2 faces, 0 solids (baked)
FEATURE [Part::Part2DObjectPython] Rectangle093  # Draft 2D object (typed FeaturePython)
  ChamferSize = 0
  Columns = 1
  FilletRadius = 0
  Height = 950
  Length = 950
  MakeFace = true
  Placement = pos=(390.401,2825.38,0) rot=(0.707107,0.707107,0;3.14159rad)
  Rows = 1
FEATURE [Part::Feature] mirror052  label="Mirror of Sofa - 017"
  Placement = pos=(-17762.3,-3499.15,0) rot=(0,0,1;0rad)
  shape: bbox 1883 x 750 x 2e-07 mm, 2 faces, 0 solids (baked)
FEATURE [Part::Feature] mirror053  label="Mirror of Bed-Double005"
  Placement = pos=(-2125.14,1590.4,0) rot=(0,0,1;0rad)
  shape: bbox 1400 x 1900 x 2e-07 mm, 4 faces, 0 solids (baked)
FEATURE [Part::Part2DObjectPython] Rectangle094  # Draft 2D object (typed FeaturePython)
  ChamferSize = 0
  Columns = 18
  FilletRadius = 0
  Height = 2250
  Length = 2211.32
  MakeFace = false
  Placement = pos=(17670.3,-160,0) rot=(0.707107,0.707107,0;3.14159rad)
  Rows = 1
FEATURE [Part::Feature] Compound055  label="dinning004"
  Placement = pos=(-1210.3,-14381.2,0) rot=(0,0,1;1.5708rad)
  shape: bbox 1200 x 2057 x 2e-07 mm, 5 faces, 0 solids (baked)
FEATURE [Part::Feature] mirror062  label="Mirror of Compound059"
  Placement = pos=(4548.65,3195.2,0) rot=(0,0,1;0rad)
  shape: bbox 1907 x 2554 x 2e-07 mm, 7 faces, 0 solids (baked)
FEATURE [Part::Feature] mirror066  label="Mirror of Compound060"
  Placement = pos=(-1907.09,0,0) rot=(0,0,1;0rad)
  shape: bbox 1907 x 2554 x 2e-07 mm, 7 faces, 0 solids (baked)
FEATURE [Part::Part2DObjectPython] Rectangle102  # Draft 2D object (typed FeaturePython)
  ChamferSize = 0
  Columns = 1
  FilletRadius = 0
  Height = 1746.46
  Length = 1189.19
  MakeFace = true
  Placement = pos=(1661.54,6302.77,0) rot=(0.707107,0.707107,0;3.14159rad)
  Rows = 1
FEATURE [Part::Feature] mirror071  label="Mirror of Mirror of 90cm door010"
  Placement = pos=(-156.608,3268.49,0) rot=(0,0,1;0rad)
  shape: bbox 1000 x 972 x 2e-07 mm, 5 faces, 0 solids (baked)
FEATURE [Part::Feature] Compound058  label="90cm door006"
  Placement = pos=(8429.63,-2705.28,0) rot=(0,0,1;1.5708rad)
  shape: bbox 1000 x 972 x 2e-07 mm, 5 faces, 0 solids (baked)
FEATURE [Part::Feature] Compound061  label="Compound050"
  Placement = pos=(-951.5,6012.83,0) rot=(0,0,1;0rad)
  shape: bbox 2057 x 1950 x 2e-07 mm, 7 faces, 0 solids (baked)
FEATURE [Part::Mirroring] mirror084  label="Mirror of Door-90cm007"
  Base = (4121.31,-1938.87,0)
  Normal = (-1,0,0)
FEATURE [Part::Part2DObjectPython] Rectangle113  # Draft 2D object (typed FeaturePython)
  ChamferSize = 0
  Columns = 13
  FilletRadius = 0
  Height = 1595.64
  Length = 1037.23
  MakeFace = false
  Placement = pos=(1661.54,6302.77,0) rot=(0.707107,0.707107,0;3.14159rad)
  Rows = 1
FEATURE [Part::Feature] mirror088  label="Mirror of Mirror of Mirror of 90cm door007"
  Placement = pos=(-6324.81,751.517,0) rot=(0,0,1;0rad)
  shape: bbox 1000 x 972 x 2e-07 mm, 5 faces, 0 solids (baked)
FEATURE [Part::Feature] mirror090  label="Mirror of Mirror of 90cm door013"
  Placement = pos=(-23936.2,-2627.64,0) rot=(0,0,1;0rad)
  shape: bbox 1000 x 972 x 2e-07 mm, 5 faces, 0 solids (baked)
FEATURE [Part::Feature] mirror091  label="Mirror of 90cm door008"
  Placement = pos=(-35773.7,-3233,0) rot=(0,0,1;0rad)
  shape: bbox 1000 x 972 x 2e-07 mm, 5 faces, 0 solids (baked)
FEATURE [Part::Feature] mirror092  label="Mirror of Mirror of 90cm door014"
  Placement = pos=(-23936.2,-2627.64,0) rot=(0,0,1;0rad)
  shape: bbox 1000 x 972 x 2e-07 mm, 5 faces, 0 solids (baked)
FEATURE [Part::Feature] mirror094  label="Mirror of 90cm door009"
  Placement = pos=(-18703.5,21483.8,0) rot=(0,0,-1;1.5708rad)
  shape: bbox 972 x 1000 x 2e-07 mm, 5 faces, 0 solids (baked)
FEATURE [Part::Feature] mirror095  label="Mirror of Mirror of 90cm door016"
  Placement = pos=(-18098.2,9646.33,0) rot=(0,0,-1;1.5708rad)
  shape: bbox 972 x 1000 x 2e-07 mm, 5 faces, 0 solids (baked)
FEATURE [Part::Feature] mirror096  label="Mirror of Mirror of Mirror of 90cm door009"
  Placement = pos=(-18098.2,9646.33,0) rot=(0,0,-1;1.5708rad)
  shape: bbox 972 x 1000 x 2e-07 mm, 5 faces, 0 solids (baked)
FEATURE [App::Annotation] Text002
  LabelText = 90cm Door Bank 
  Position = (-17039.1,-18.7112,0)
FEATURE [Part::Part2DObjectPython] Rectangle114  # Draft 2D object (typed FeaturePython)
  ChamferSize = 0
  Columns = 1
  FilletRadius = 0
  Height = 1595.64
  Length = 146.163
  MakeFace = false
  Placement = pos=(1661.54,6302.77,0) rot=(0,0,-1;1.5708rad)
  Rows = 1
FEATURE [Part::Part2DObjectPython] Rectangle115  # Draft 2D object (typed FeaturePython)
  ChamferSize = 0
  Columns = 1
  FilletRadius = 0
  Height = 7802.78
  Length = 2801.63
  MakeFace = false
  Placement = pos=(3257.19,-310.814,0) rot=(0,0,1;0rad)
  Rows = 1
FEATURE [Part::Part2DObjectPython] Rectangle116  # Draft 2D object (typed FeaturePython)
  ChamferSize = 0
  Columns = 1
  FilletRadius = 0
  Height = 600
  Length = 2500
  MakeFace = true
  Placement = pos=(3408,3240,0) rot=(0,0,1;0rad)
  Rows = 1
FEATURE [Part::Part2DObjectPython] Rectangle117  # Draft 2D object (typed FeaturePython)
  ChamferSize = 0
  Columns = 1
  FilletRadius = 0
  Height = 3249.19
  Length = 2500
  MakeFace = true
  Placement = pos=(3408,-160,0) rot=(0,0,1;0rad)
  Rows = 1
FEATURE [Part::Part2DObjectPython] Rectangle119  # Draft 2D object (typed FeaturePython)
  ChamferSize = 0
  Columns = 1
  FilletRadius = 0
  Height = 4100
  Length = 2500
  MakeFace = true
  Placement = pos=(3408,3240,0) rot=(0,0,1;0rad)
  Rows = 1
FEATURE [Part::Part2DObjectPython] Rectangle120  # Draft 2D object (typed FeaturePython)
  ChamferSize = 0
  Columns = 1
  FilletRadius = 0
  Height = 4401.63
  Length = 2801.63
  MakeFace = true
  Placement = pos=(3257.19,3089.19,0) rot=(0,0,1;0rad)
  Rows = 1
FEATURE [Part::Part2DObjectPython] Rectangle121  # Draft 2D object (typed FeaturePython)
  ChamferSize = 0
  Columns = 1
  FilletRadius = 0
  Height = 3550.81
  Length = 2801.63
  MakeFace = true
  Placement = pos=(3257.19,-310.814,0) rot=(0,0,1;0rad)
  Rows = 1
FEATURE [Part::Feature] Compound064  label="Sofa - 010"
  Placement = pos=(-4732.17,-2088.69,0) rot=(0,0,1;1.5708rad)
  shape: bbox 750 x 1400 x 2e-07 mm, 2 faces, 0 solids (baked)
FEATURE [Part::Part2DObjectPython] Rectangle122  # Draft 2D object (typed FeaturePython)
  ChamferSize = 0
  Columns = 1
  FilletRadius = 0
  Height = 600
  Length = 2500
  MakeFace = true
  Placement = pos=(3408,2489.19,0) rot=(0,0,1;0rad)
  Rows = 1
FEATURE [Part::Part2DObjectPython] Line025  # Draft 2D object (typed FeaturePython)
  ChamferSize = 0
  Closed = false
  End = (5908,2789.19,0)
  FilletRadius = 0
  Length = 2500
  MakeFace = true
  Placement = pos=(549.567,-4250.81,0) rot=(0,0,1;0rad)
  Points = (2) [(2858.43,7040,0),(5358.43,7040,0)]
  Start = (3408,2789.19,0)
  Subdivisions = 0
FEATURE [Part::Feature] mirror104  label="Mirror of Sink 008"
  Placement = pos=(4722.56,22170.2,0) rot=(0,0,-1;1.5708rad)
  shape: bbox 500 x 300 x 2e-07 mm, 3 faces, 0 solids (baked)
FEATURE [Part::Part2DObjectPython] Rectangle125  # Draft 2D object (typed FeaturePython)
  ChamferSize = 0
  Columns = 1
  FilletRadius = 0
  Height = 2500
  Length = 600.001
  MakeFace = true
  Placement = pos=(21070.3,8590,0) rot=(0,0,1;0rad)
  Rows = 1
FEATURE [Part::Feature] Clone001  label="Clone of Door-90cm004"
  Placement = pos=(17661.8,8116.14,0) rot=(0,0,1;0rad)
  shape: bbox 972 x 1000 x 2e-07 mm, 5 faces, 0 solids (baked)
FEATURE [Part::Part2DObjectPython] Rectangle127  # Draft 2D object (typed FeaturePython)
  ChamferSize = 0
  Columns = 1
  FilletRadius = 0
  Height = 2015.84
  Length = 150.814
  MakeFace = false
  Placement = pos=(21070.3,6422.44,0) rot=(0,0,1;0rad)
  Rows = 1
FEATURE [Part::Part2DObjectPython] Rectangle128  # Draft 2D object (typed FeaturePython)
  ChamferSize = 0
  Columns = 1
  FilletRadius = 0
  Height = 4000
  Length = 2500
  MakeFace = true
  Placement = pos=(17670.3,8590,0) rot=(0.707107,0.707107,0;3.14159rad)
  Rows = 1
FEATURE [Part::Extrusion] Extrusion
  Base = -> Rectangle128
  Dir = (0,0,2198.29)
  DirMode = 0
  FaceMakerClass = Part::FaceMakerBullseye
  LengthFwd = 0
  LengthRev = 0
  Solid = true
  Symmetric = false
FEATURE [Part::Thickness] Thickness
  Faces = -> Extrusion [Face3,Face1]
  Intersection = false
  Join = 2
  Mode = 0
  SelfIntersection = false
  Value = 150
FEATURE [Part::Part2DObjectPython] Rectangle129  # Draft 2D object (typed FeaturePython)
  ChamferSize = 0
  Columns = 1
  FilletRadius = 0
  Height = 2500
  Length = 4000
  MakeFace = true
  Placement = pos=(17670.3,8590,0) rot=(0,0,1;0rad)
  Rows = 1
FEATURE [Part::Extrusion] Extrusion001
  Base = -> Rectangle129
  Dir = (0,0,2200)
  DirMode = 0
  FaceMakerClass = Part::FaceMakerBullseye
  LengthFwd = 0
  LengthRev = 0
  Solid = true
  Symmetric = false
FEATURE [Part::Part2DObjectPython] Line027  # Draft 2D object (typed FeaturePython)
  ChamferSize = 0
  Closed = false
  End = (17970.3,2237.32,0)
  FilletRadius = 0
  Length = 2923.45
  MakeFace = true
  Placement = pos=(35940.6,7398.1,0) rot=(0,0,1;3.14159rad)
  Points = (2) [(17970.3,2237.32,0),(17970.3,5160.77,0)]
  Start = (17970.3,5160.77,0)
  Subdivisions = 0
FEATURE [Part::Feature] mirror105  label="Mirror of 90cm door010"
  Placement = pos=(199.999,-2859.2,0) rot=(0,0,1;0rad)
  shape: bbox 1000 x 972 x 2e-07 mm, 5 faces, 0 solids (baked)
FEATURE [Part::Part2DObjectPython] Line029  # Draft 2D object (typed FeaturePython)
  ChamferSize = 0
  Closed = false
  End = (3408,6712,0)
  FilletRadius = 0
  Length = 2500
  MakeFace = true
  Points = (2) [(5908,6712,0),(3408,6712,0)]
  Start = (5908,6712,0)
  Subdivisions = 0
FEATURE [Part::Feature] mirror107  label="Mirror of Mirror of 90cm door017"
  Placement = pos=(-1083.97,14135.6,0) rot=(0,0,-1;1.5708rad)
  shape: bbox 972 x 1000 x 2e-07 mm, 5 faces, 0 solids (baked)
FEATURE [Part::Part2DObjectPython] Rectangle131  # Draft 2D object (typed FeaturePython)
  ChamferSize = 0
  Columns = 1
  FilletRadius = 0
  Height = 1449.19
  Length = 150.814
  MakeFace = false
  Placement = pos=(3257.19,-160,0) rot=(0,0,1;0rad)
  Rows = 1
FEATURE [Part::Feature] mirror  label="Mirror of 90cm door011"
  Placement = pos=(-1689.34,21009.5,0) rot=(0,0,-1;1.5708rad)
  shape: bbox 972 x 1000 x 2e-07 mm, 5 faces, 0 solids (baked)
FEATURE [Part::Feature] mirror108  label="Mirror of Mirror of 90cm door018"
  Placement = pos=(-3027.97,9171.99,0) rot=(0,0,-1;1.5708rad)
  shape: bbox 972 x 1000 x 2e-07 mm, 5 faces, 0 solids (baked)
FEATURE [Part::Feature] mirror109  label="Mirror of Sofa - 018"
  Placement = pos=(-672.292,15080.2,0) rot=(0,0,-1;1.5708rad)
  shape: bbox 750 x 1883 x 2e-07 mm, 2 faces, 0 solids (baked)
FEATURE [Part::Feature] mirror110  label="Mirror of Sofa - 019"
  Placement = pos=(-13673.5,-9191.81,0) rot=(0,0,1;0rad)
  shape: bbox 1400 x 750 x 2e-07 mm, 2 faces, 0 solids (baked)
FEATURE [Part::Part2DObjectPython] Rectangle136  # Draft 2D object (typed FeaturePython)
  ChamferSize = 0
  Columns = 1
  FilletRadius = 0
  Height = 9000
  Length = 5000
  MakeFace = false
  MapMode = -1
  Placement = pos=(9194.87,-20267.6,0) rot=(0,0,1;0rad)
  Rows = 1
FEATURE [Part::Part2DObjectPython] Rectangle139  # Draft 2D object (typed FeaturePython)
  ChamferSize = 0
  Columns = 1
  FilletRadius = 0
  Height = 600
  Length = 2400
  MakeFace = true
  Placement = pos=(9794.87,-15414.9,0) rot=(0,0,1;1.5708rad)
  Rows = 1
FEATURE [Part::Feature] Compound065  label="Sink 003"
  Placement = pos=(3881.67,-13417.7,0) rot=(0,0,1;0rad)
  shape: bbox 300 x 500 x 2e-07 mm, 3 faces, 0 solids (baked)
FEATURE [Part::Part2DObjectPython] Rectangle140  # Draft 2D object (typed FeaturePython)
  ChamferSize = 0
  Columns = 1
  FilletRadius = 0
  Height = 1600
  Length = 2605.46
  MakeFace = false
  Placement = pos=(9194.87,-12867.6,0) rot=(0,0,1;0rad)
  Rows = 1
FEATURE [Part::Part2DObjectPython] Rectangle141  # Draft 2D object (typed FeaturePython)
  ChamferSize = 0
  Columns = 1
  FilletRadius = 0
  Height = 1894.44
  Length = 2899.9
  MakeFace = false
  Placement = pos=(9047.65,-13014.9,0) rot=(0,0,1;0rad)
  Rows = 1
FEATURE [Part::Feature] Compound067  label="Door-90cm008"
  Placement = pos=(7359.39,-13341.5,0) rot=(0,0,1;0rad)
  shape: bbox 972 x 1000 x 2e-07 mm, 5 faces, 0 solids (baked)
FEATURE [Part::Part2DObjectPython] Rectangle142  # Draft 2D object (typed FeaturePython)
  ChamferSize = 0
  Columns = 1
  FilletRadius = 0
  Height = 1747.22
  Length = 146.164
  MakeFace = false
  Placement = pos=(10767.9,-13014.9,0) rot=(0,0,1;0rad)
  Rows = 1
FEATURE [Part::Part2DObjectPython] Line030  # Draft 2D object (typed FeaturePython)
  ChamferSize = 0
  Closed = false
  End = (9494.87,-13014.9,0)
  FilletRadius = 0
  Length = 2400
  MakeFace = true
  Placement = pos=(0,-20107.6,0) rot=(0,0,1;0rad)
  Points = (2) [(9494.87,4692.78,0),(9494.87,7092.78,0)]
  Start = (9494.87,-15414.9,0)
  Subdivisions = 0
FEATURE [Part::Part2DObjectPython] Rectangle143  # Draft 2D object (typed FeaturePython)
  ChamferSize = 0
  Columns = 1
  FilletRadius = 0
  Height = 600
  Length = 146.164
  MakeFace = false
  Placement = pos=(9194.87,-15414.9,0) rot=(0,0,-1;1.5708rad)
  Rows = 1
FEATURE [Part::Part2DObjectPython] Rectangle144  # Draft 2D object (typed FeaturePython)
  ChamferSize = 0
  Columns = 13
  FilletRadius = 0
  Height = 1573.06
  Length = 1600
  MakeFace = false
  Placement = pos=(9194.87,-12867.6,0) rot=(0.707107,0.707107,0;3.14159rad)
  Rows = 1
FEATURE [Part::Feature] mirror115  label="Mirror of Sofa - 021"
  Placement = pos=(-8834.23,-22581.1,0) rot=(0,0,1;0rad)
  shape: bbox 1400 x 750 x 2e-07 mm, 2 faces, 0 solids (baked)
FEATURE [Part::Feature] mirror121  label="Mirror of Rectangle139"
  Placement = pos=(-972,7.29e-10,0) rot=(0,0,1;0rad)
  shape: bbox 2247 x 1600 x 2e-07 mm, 0 faces, 0 solids (baked)
FEATURE [Part::Feature] mirror122  label="Mirror of Rectangle140"
  Placement = pos=(-972,7.29e-10,0) rot=(0,0,1;0rad)
  shape: bbox 2542 x 1894 x 2e-07 mm, 0 faces, 0 solids (baked)
FEATURE [Part::Feature] mirror123  label="Mirror of Mirror of Sink 010"
  Placement = pos=(-972,7.29e-10,0) rot=(0,0,1;0rad)
  shape: bbox 500 x 300 x 2e-07 mm, 3 faces, 0 solids (baked)
FEATURE [Part::Feature] mirror127  label="Mirror of Door-90cm012"
  Placement = pos=(972,-7.29e-10,0) rot=(0,0,1;0rad)
  shape: bbox 972 x 1000 x 2e-07 mm, 5 faces, 0 solids (baked)
FEATURE [Part::Part2DObjectPython] Line031  # Draft 2D object (typed FeaturePython)
  ChamferSize = 0
  Closed = false
  End = (14194.9,-15414.9,0)
  FilletRadius = 0
  Length = 4400
  MakeFace = true
  Points = (2) [(9794.87,-15414.9,0),(14194.9,-15414.9,0)]
  Start = (9794.87,-15414.9,0)
  Subdivisions = 0
FEATURE [Part::Part2DObjectPython] Line032  # Draft 2D object (typed FeaturePython)
  ChamferSize = 0
  Closed = false
  End = (9794.87,-16536.6,0)
  FilletRadius = 0
  Length = 1121.73
  MakeFace = true
  Points = (2) [(9794.87,-15414.9,0),(9794.87,-16536.6,0)]
  Start = (9794.87,-15414.9,0)
  Subdivisions = 0
FEATURE [Part::Part2DObjectPython] Line033  # Draft 2D object (typed FeaturePython)
  ChamferSize = 0
  Closed = false
  End = (10998.5,-16536.6,0)
  FilletRadius = 0
  Length = 3521.73
  MakeFace = true
  Points = (2) [(10998.5,-13014.9,0),(10998.5,-16536.6,0)]
  Start = (10998.5,-13014.9,0)
  Subdivisions = 0
FEATURE [Part::Mirroring] mirror128  label="Mirror of Mirror of Mirror of WC007"
  Base = (15617.4,-12067.6,0)
  Normal = (0,1,0)
FEATURE [Part::Mirroring] mirror129  label="Mirror of Mirror of Shower006"
  Base = (15617.4,-12067.6,0)
  Normal = (0,1,0)
FEATURE [Part::Part2DObjectPython] Line034  # Draft 2D object (typed FeaturePython)
  ChamferSize = 0
  Closed = false
  End = (15617.4,-20267.6,0)
  FilletRadius = 0
  Length = 7252.78
  MakeFace = true
  Points = (2) [(15617.4,-13014.9,0),(15617.4,-20267.6,0)]
  Start = (15617.4,-13014.9,0)
  Subdivisions = 0
FEATURE [Part::Part2DObjectPython] Line035  # Draft 2D object (typed FeaturePython)
  ChamferSize = 0
  Closed = false
  End = (15470.2,-20267.6,0)
  FilletRadius = 0
  Length = 7400
  MakeFace = true
  Points = (2) [(15470.2,-12867.6,0),(15470.2,-20267.6,0)]
  Start = (15470.2,-12867.6,0)
  Subdivisions = 0
FEATURE [Part::Part2DObjectPython] Rectangle147  # Draft 2D object (typed FeaturePython)
  ChamferSize = 0
  Columns = 1
  FilletRadius = 0
  Height = 4100
  Length = 2500
  MakeFace = true
  Placement = pos=(11370.2,-20267.6,0) rot=(0.707107,0.707107,0;3.14159rad)
  Rows = 1
  Support = -> [mirror115]
FEATURE [Part::Feature] Compound070  label="Bed-Double006"
  Placement = pos=(13768.3,-14771.1,0) rot=(0,0,1;1.5708rad)
  shape: bbox 1900 x 1400 x 2e-07 mm, 4 faces, 0 solids (baked)
FEATURE [Part::Part2DObjectPython] Rectangle148  # Draft 2D object (typed FeaturePython)
  ChamferSize = 0
  Columns = 1
  FilletRadius = 0
  Height = 600
  Length = 2500
  MakeFace = true
  Placement = pos=(15470.2,-20267.6,0) rot=(0,0,1;1.5708rad)
  Rows = 1
FEATURE [Part::Part2DObjectPython] Rectangle149  # Draft 2D object (typed FeaturePython)
  ChamferSize = 0
  Columns = 1
  FilletRadius = 0
  Height = 4752.78
  Length = 972
  MakeFace = true
  Placement = pos=(13222.9,-17767.6,0) rot=(0,0,1;0rad)
  Rows = 1
FEATURE [Part::Feature] Compound071  label="Sofa - 011"
  Placement = pos=(11288.8,-13897.5,0) rot=(0,0,1;0rad)
  shape: bbox 1883 x 750 x 2e-07 mm, 2 faces, 0 solids (baked)
FEATURE [Part::Feature] Compound072  label="Sofa - 012"
  Placement = pos=(7557.79,-14611,0) rot=(0,0,1;1.5708rad)
  shape: bbox 750 x 1400 x 2e-07 mm, 2 faces, 0 solids (baked)
FEATURE [Part::Feature] Compound074  label="dinning008"
  Placement = pos=(38896.5,-9873.61,0) rot=(0,0,1;3.14159rad)
  shape: bbox 2057 x 1200 x 2e-07 mm, 5 faces, 0 solids (baked)
FEATURE [Sketcher::SketchObject] Sketch
  sketch-geometry (13):
    g0: GeomPoint [constr] X=777.55 Y=-3734.3 Z=0
    g1: GeomPoint [constr] X=2549.74 Y=-3772.61 Z=0
    g2: GeomPoint [constr] X=289.001 Y=-5334.05 Z=0
    g3: GeomPoint [constr] X=2262.35 Y=-5516.06 Z=0
    g4: LineSegment StartX=289.001 StartY=-5334.05 StartZ=0 EndX=569.618 EndY=-4182.1 EndZ=0
    g5-g9: Circle [constr] x5 (B-spline internal-alignment scaffolding for g10; pole/knot coordinates omitted)
    g10: BSplineCurve PolesCount=5 KnotsCount=3 Degree=3 IsPeriodic=0
    g11: LineSegment StartX=569.618 StartY=-4182.1 StartZ=0 EndX=3492.32 EndY=-3505.46 EndZ=0
    g12: LineSegment StartX=4416.21 StartY=-5096.69 StartZ=0 EndX=3492.32 EndY=-3505.46 EndZ=0
  constraints (10):
    c: Coincident(g4,g2)
    c: Coincident(g5,g2)
    c: Radius(g5) = 500
    c: Equal(g5, g6-g9) x4
    c: InternalAlignment(g5-g9 -> g10) x5
    c: Coincident(g12,g9)
    c: Coincident(g11,g12)
    c: Coincident(g4,g11)
    c: Distance(g11) = 3000  'diagon'
    c: Distance(g12) = 1840
FEATURE [Part::Part2DObjectPython] DWire  # Draft 2D object (typed FeaturePython)
  Base = -> Sketch
  ChamferSize = 0
  Closed = true
  End = (4416.21,-5096.69,0)
  FilletRadius = 0
  Length = 10159.7
  MakeFace = true
  Points = (4) [(289.001,-5334.05,0),(569.618,-4182.1,0),(3492.32,-3505.46,0),(4416.21,-5096.69,0)]
  Start = (289.001,-5334.05,0)
  Subdivisions = 0
FEATURE [Part::FeaturePython] Equipment  # WARN: FeaturePython — macro-defined, semantics opaque (R4)
  EquipmentPower = 0
  HorizontalArea = 0
  MoveWithHost = false
  PerimeterLength = 0
  Role = 0
  VerticalArea = 0
FEATURE [App::DocumentObjectGroup] Group004  label="Plan Layout 1"
  Group = -> [Compound030,Shell002,Compound027,Rectangle075,Rectangle079,Rectangle090,Compound052,Rectangle093,mirror052,mirror066,Rectangle102,mirror071,Compound061,Rectangle113,mirror088,Rectangle114,Rectangle115,Rectangle116,Rectangle117,Rectangle119,Rectangle120,Rectangle121,Rectangle122,Line025,mirror104,Line029,mirror107,Rectangle131,mirror,mirror108,Equipment]
FEATURE [App::DocumentObjectGroup] Group  label="7.5mx6m"
  Group = -> [Dimension,Dimension001,Rectangle,Group004]
FEATURE [Part::Feature] mirror130  label="Mirror of Mirror of Mirror of 90cm door010"
  Placement = pos=(12987.5,-2103.84,0) rot=(0,0,1;0rad)
  shape: bbox 1000 x 972 x 2e-07 mm, 5 faces, 0 solids (baked)
FEATURE [Part::Part2DObjectPython] Line036  # Draft 2D object (typed FeaturePython)
  ChamferSize = 0
  Closed = false
  End = (20820.3,6422.44,0)
  FilletRadius = 0
  Length = 3213.12
  MakeFace = true
  Points = (2) [(20820.3,3209.32,0),(20820.3,6422.44,0)]
  Start = (20820.3,3209.32,0)
  Subdivisions = 0
FEATURE [Part::Part2DObjectPython] Rectangle150  # Draft 2D object (typed FeaturePython)
  ChamferSize = 0
  Columns = 1
  FilletRadius = 0
  Height = 11250
  Length = 4000
  MakeFace = false
  MapMode = -1
  Placement = pos=(17618.1,7369.69,0) rot=(0,0,-1;1.5708rad)
  Rows = 1
FEATURE [Part::Feature] mirror136  label="Mirror of Mirror of WC006"
  Placement = pos=(16340.8,42674.9,0) rot=(0,0,-1;1.5708rad)
  shape: bbox 370 x 660 x 2e-07 mm, 2 faces, 0 solids (baked)
FEATURE [Part::Feature] mirror137  label="Mirror of Mirror of Sink 012"
  Placement = pos=(16340.8,42674.9,0) rot=(0,0,-1;1.5708rad)
  shape: bbox 300 x 500 x 2e-07 mm, 3 faces, 0 solids (baked)
FEATURE [Part::Feature] mirror138  label="Mirror of Mirror of Shower007"
  Placement = pos=(16340.8,42674.9,0) rot=(0,0,-1;1.5708rad)
  shape: bbox 800 x 800 x 2e-07 mm, 2 faces, 0 solids (baked)
FEATURE [Part::Feature] Compound075  label="90cm door007"
  Placement = pos=(15809.5,4648.51,0) rot=(0,0,1;0rad)
  shape: bbox 972 x 1000 x 2e-07 mm, 5 faces, 0 solids (baked)
FEATURE [Part::Part2DObjectPython] Rectangle151  # Draft 2D object (typed FeaturePython)
  ChamferSize = 0
  Columns = 1
  FilletRadius = 0
  Height = 153.543
  Length = 600
  MakeFace = false
  Placement = pos=(19218.1,3969.69,0) rot=(0,0,-1;1.5708rad)
  Rows = 1
FEATURE [Part::Part2DObjectPython] Line037  # Draft 2D object (typed FeaturePython)
  ChamferSize = 0
  Closed = false
  End = (19218.1,3969.69,0)
  FilletRadius = 0
  Length = 1000
  MakeFace = true
  Placement = pos=(17778.1,36636.4,0) rot=(0,0,-1;1.5708rad)
  Points = (2) [(32666.7,440,0),(32666.7,1440,0)]
  Start = (18218.1,3969.69,0)
  Subdivisions = 0
FEATURE [Part::Part2DObjectPython] Line039  # Draft 2D object (typed FeaturePython)
  ChamferSize = 0
  Closed = false
  End = (18218.1,3969.69,0)
  FilletRadius = 0
  Length = 999.133
  MakeFace = true
  Placement = pos=(17778.1,36636.4,0) rot=(0,0,-1;1.5708rad)
  Points = (2) [(31667.6,440,0),(32666.7,440,0)]
  Start = (18218.1,4968.82,0)
  Subdivisions = 0
FEATURE [Part::Feature] Compound076  label="Sink 004"
  Placement = pos=(21574.3,13282.9,0) rot=(0,0,-1;1.5708rad)
  shape: bbox 500 x 300 x 2e-07 mm, 3 faces, 0 solids (baked)
FEATURE [Part::Part2DObjectPython] Line040  # Draft 2D object (typed FeaturePython)
  ChamferSize = 0
  Closed = false
  End = (21977.1,7669.69,0)
  FilletRadius = 0
  Length = 2605.46
  MakeFace = true
  Placement = pos=(14884.3,17164.6,0) rot=(0,0,-1;1.5708rad)
  Points = (2) [(9494.87,4487.32,0),(9494.87,7092.78,0)]
  Start = (19371.6,7669.69,0)
  Subdivisions = 0
FEATURE [Part::Part2DObjectPython] Rectangle152  # Draft 2D object (typed FeaturePython)
  ChamferSize = 0
  Columns = 1
  FilletRadius = 0
  Height = 600
  Length = 2605.46
  MakeFace = true
  Placement = pos=(19371.6,7369.69,0) rot=(0,0,1;0rad)
  Rows = 1
FEATURE [Part::Part2DObjectPython] Rectangle153  # Draft 2D object (typed FeaturePython)
  ChamferSize = 0
  Columns = 1
  FilletRadius = 0
  Height = 800
  Length = 1800.87
  MakeFace = true
  Placement = pos=(21177.1,7369.69,0) rot=(0,0,-1;1.5708rad)
  Rows = 1
FEATURE [Part::Part2DObjectPython] Rectangle154  # Draft 2D object (typed FeaturePython)
  ChamferSize = 0
  Columns = 1
  FilletRadius = 0
  Height = 450
  Length = 450
  MakeFace = true
  Placement = pos=(31217.6,4396.25,0) rot=(0,0,1;0rad)
  Rows = 1
  Support = -> [Compound051]
FEATURE [Part::FeaturePython] Array  # Draft array (typed FeaturePython)
  Angle = 360
  ArrayType = 0
  Axis = (0,0,1)
  Base = -> Rectangle154
  Center = (0,0,0)
  Fuse = false
  IntervalAxis = (0,0,0)
  IntervalX = (-650,0,0)
  IntervalY = (0,0,0)
  IntervalZ = (0,0,0)
  NumberPolar = 1
  NumberX = 3
  NumberY = 0
  NumberZ = 0
  Placement = pos=(17778.1,37236.4,0) rot=(0,0,-1;1.5708rad)
FEATURE [Part::Part2DObjectPython] DWire008  # Draft 2D object (typed FeaturePython)
  ChamferSize = 0
  Closed = true
  End = (19218.1,3969.69,0)
  FilletRadius = 0
  Length = 23193.2
  MakeFace = true
  Placement = pos=(17778.1,36636.4,0) rot=(0,0,-1;1.5708rad)
  Points = (16) [(32666.7,1593.54,0),(33420.3,1593.54,0),(33420.3,-313.543,0),(29113.2,-313.543,0),(29113.2,1593.54,0),(31667.6,1593.54,0),(31667.6,1440,0),+9 more]
  Start = (19371.6,3969.69,0)
  Subdivisions = 0
FEATURE [Part::Part2DObjectPython] DWire009  # Draft 2D object (typed FeaturePython)
  ChamferSize = 0
  Closed = true
  End = (18218.1,3969.69,0)
  FilletRadius = 0
  Length = 6398.27
  MakeFace = true
  Placement = pos=(17778.1,36636.4,0) rot=(0,0,-1;1.5708rad)
  Points = (6) [(32666.7,1440,0),(33266.7,1440,0),(33266.7,-160,0),(31667.6,-160,0),(31667.6,440,0),(32666.7,440,0)]
  Start = (19218.1,3969.69,0)
  Subdivisions = 0
FEATURE [Part::Feature] Compound077  label="Bed-Double007"
  Placement = pos=(31459.1,6248.3,0) rot=(0,0,1;0rad)
  shape: bbox 1400 x 1900 x 2e-07 mm, 4 faces, 0 solids (baked)
FEATURE [Part::Part2DObjectPython] Rectangle157  # Draft 2D object (typed FeaturePython)
  ChamferSize = 0
  Columns = 1
  FilletRadius = 0
  Height = 3000
  Length = 4000
  MakeFace = true
  Placement = pos=(25868.1,7369.69,0) rot=(0,0,-1;1.5708rad)
  Rows = 1
FEATURE [Part::Part2DObjectPython] Rectangle158  # Draft 2D object (typed FeaturePython)
  ChamferSize = 0
  Columns = 1
  FilletRadius = 0
  Height = 3303.44
  Length = 4303.44
  MakeFace = true
  Placement = pos=(25716.3,7521.41,0) rot=(0,0,-1;1.5708rad)
  Rows = 1
FEATURE [Part::Part2DObjectPython] Rectangle161  # Draft 2D object (typed FeaturePython)
  ChamferSize = 0
  Columns = 1
  FilletRadius = 0
  Height = 600.001
  Length = 18
  MakeFace = true
  Placement = pos=(28268.1,4887.69,0) rot=(0,0,-1;1.5708rad)
  Rows = 1
FEATURE [Part::Part2DObjectPython] Rectangle163  # Draft 2D object (typed FeaturePython)
  ChamferSize = 0
  Columns = 1
  FilletRadius = 0
  Height = 600.001
  Length = 18
  MakeFace = true
  Placement = pos=(28268.1,4905.69,0) rot=(0,0,-1;1.5708rad)
  Rows = 1
FEATURE [Part::Part2DObjectPython] Rectangle166  # Draft 2D object (typed FeaturePython)
  ChamferSize = 0
  Columns = 1
  FilletRadius = 0
  Height = 6344.73
  Length = 4000
  MakeFace = true
  Placement = pos=(19371.6,7969.69,0) rot=(0,0,-1;1.5708rad)
  Rows = 1
FEATURE [Part::Part2DObjectPython] Rectangle167  # Draft 2D object (typed FeaturePython)
  ChamferSize = 0
  Columns = 1
  FilletRadius = 0
  Height = 6651.82
  Length = 4307.09
  MakeFace = true
  Placement = pos=(19218.1,8123.23,0) rot=(0,0,-1;1.5708rad)
  Rows = 1
FEATURE [Part::Feature] Clone002  label="Clone of Door-90cm006"
  Placement = pos=(25396,7378.23,0) rot=(0,0,-1;1.5708rad)
  shape: bbox 1000 x 972 x 2e-07 mm, 5 faces, 0 solids (baked)
FEATURE [Part::Feature] Compound078  label="Sofa - 013"
  Placement = pos=(27405.7,5571.74,0) rot=(0,0,-1;1.5708rad)
  shape: bbox 750 x 1883 x 2e-07 mm, 2 faces, 0 solids (baked)
FEATURE [Part::Feature] mirror139  label="Mirror of Sofa - 022"
  Placement = pos=(42414.5,13130.5,0) rot=(0,0,1;3.14159rad)
  shape: bbox 1883 x 750 x 2e-07 mm, 2 faces, 0 solids (baked)
FEATURE [Part::Part2DObjectPython] Rectangle168  # Draft 2D object (typed FeaturePython)
  ChamferSize = 0
  Columns = 1
  FilletRadius = 0
  Height = 450
  Length = 450
  MakeFace = true
  Placement = pos=(24918.3,7704.65,0) rot=(0,0,-1;1.10715rad)
  Rows = 1
FEATURE [Part::Part2DObjectPython] Rectangle169  # Draft 2D object (typed FeaturePython)
  ChamferSize = 0
  Columns = 1
  FilletRadius = 0
  Height = 950
  Length = 950
  MakeFace = true
  Placement = pos=(23477.9,6668.08,0) rot=(1,0,0;3.14159rad)
  Rows = 1
FEATURE [Part::Part2DObjectPython] DWire010  # Draft 2D object (typed FeaturePython)
  ChamferSize = 0
  Closed = true
  End = (25869.9,8123.23,0)
  FilletRadius = 0
  Length = 34121.1
  MakeFace = true
  Placement = pos=(17778.1,36636.4,0) rot=(0,0,-1;1.5708rad)
  Points = (12) [(29115,8091.82,0),(29115,11241.7,0),(33418.4,11241.7,0),(33418.4,7938.28,0),(32820.3,7938.28,0),(32820.3,1593.54,0),(33420.3,1593.54,0),+5 more]
  Start = (25869.9,7521.41,0)
  Subdivisions = 0
FEATURE [Part::Part2DObjectPython] DWire011  # Draft 2D object (typed FeaturePython)
  ChamferSize = 0
  Closed = true
  End = (25716.3,7969.69,0)
  FilletRadius = 0
  Length = 32892.7
  MakeFace = true
  Placement = pos=(17778.1,36636.4,0) rot=(0,0,-1;1.5708rad)
  Points = (12) [(29268.5,7938.28,0),(29268.5,11088.2,0),(33264.9,11088.2,0),(33264.9,8091.82,0),(32666.7,8091.82,0),(32666.7,1440,0),(33266.7,1440,0),+5 more]
  Start = (25716.3,7367.87,0)
  Subdivisions = 0
FEATURE [Part::Feature] mirror145  label="Mirror of Mirror of Mirror of Mirror of 90cm door012"
  Placement = pos=(17778.1,36682.9,0) rot=(0,0,-1;1.5708rad)
  shape: bbox 972 x 1000 x 2e-07 mm, 5 faces, 0 solids (baked)
FEATURE [Part::Feature] mirror146  label="Mirror of 90cm door014"
  Placement = pos=(17778.1,36682.9,0) rot=(0,0,-1;1.5708rad)
  shape: bbox 972 x 1000 x 2e-07 mm, 5 faces, 0 solids (baked)
FEATURE [Part::Feature] mirror147  label="Mirror of Mirror of Mirror of Mirror of 90cm door013"
  Placement = pos=(17778.1,36682.9,0) rot=(0,0,-1;1.5708rad)
  shape: bbox 972 x 1000 x 2e-07 mm, 5 faces, 0 solids (baked)
FEATURE [Part::Feature] mirror148  label="Mirror of 90cm door015"
  Placement = pos=(17778.1,36682.9,0) rot=(0,0,-1;1.5708rad)
  shape: bbox 972 x 1000 x 2e-07 mm, 5 faces, 0 solids (baked)
FEATURE [Part::Part2DObjectPython] DWire012  # Draft 2D object (typed FeaturePython)
  ChamferSize = 0
  Closed = true
  End = (25716.3,3217.97,0)
  FilletRadius = 0
  Length = 22097.5
  MakeFace = true
  Placement = pos=(17778.1,36636.4,0) rot=(0,0,-1;1.5708rad)
  Points = (8) [(33418.4,9590,0),(34919,9590,0),(34919,640,0),(33420.3,640,0),(33420.3,1593.54,0),(32820.3,1593.54,0),(32820.3,7938.28,0),(33418.4,7938.28,0)]
  Start = (27368.1,3217.97,0)
  Subdivisions = 0
FEATURE [Part::Feature] mirror152  label="Mirror of Shower005"
  Placement = pos=(-356.748,4.002e-09,0) rot=(0,0,1;0rad)
  shape: bbox 800 x 800 x 2e-07 mm, 2 faces, 0 solids (baked)
FEATURE [Part::Feature] mirror153  label="Mirror of Mirror of WC008"
  Placement = pos=(-356.748,4.002e-09,0) rot=(0,0,1;0rad)
  shape: bbox 660 x 370 x 2e-07 mm, 2 faces, 0 solids (baked)
FEATURE [Part::Part2DObjectPython] DWire013  # Draft 2D object (typed FeaturePython)
  ChamferSize = 0
  Closed = true
  End = (10797.3,8840,0)
  FilletRadius = 0
  Length = 6404.88
  MakeFace = true
  Points = (6) [(10797.3,8212,0),(9794.87,8212,0),(9794.87,7240,0),(9194.87,7240,0),(9194.87,8840,0),(10797.3,8840,0)]
  Start = (10797.3,8212,0)
  Subdivisions = 0
FEATURE [Part::Part2DObjectPython] DWire014  # Draft 2D object (typed FeaturePython)
  ChamferSize = 0
  Closed = true
  End = (9194.87,7240,0)
  FilletRadius = 0
  Length = 23110.2
  MakeFace = true
  Points = (16) [(9794.87,7240,0),(9794.87,7092.78,0),(9047.65,7092.78,0),(9047.65,8987.22,0),(13338,8987.22,0),(13338,7092.78,0),(10796.3,7092.78,0),(10796.3,7240,0),+8 more]
  Start = (9794.87,7240,0)
  Subdivisions = 0
FEATURE [Part::Part2DObjectPython] Rectangle170  # Draft 2D object (typed FeaturePython)
  ChamferSize = 0
  Columns = 1
  FilletRadius = 0
  Height = 2610
  Length = 570
  MakeFace = true
  Placement = pos=(13338,7092.78,0) rot=(0,0,1;0rad)
  Rows = 1
FEATURE [Part::Feature] mirror158  label="Mirror of Mirror of Mirror of 90cm door012"
  Placement = pos=(-23936.2,-2627.64,0) rot=(0,0,1;0rad)
  shape: bbox 1000 x 972 x 2e-07 mm, 5 faces, 0 solids (baked)
FEATURE [Part::Part2DObjectPython] Rectangle173  # Draft 2D object (typed FeaturePython)
  ChamferSize = 0
  Columns = 1
  FilletRadius = 0
  Height = 2605.46
  Length = 5589.69
  MakeFace = true
  Placement = pos=(9194.87,1881.87,0) rot=(0,0,1;0rad)
  Rows = 1
FEATURE [Part::Part2DObjectPython] Rectangle177  # Draft 2D object (typed FeaturePython)
  ChamferSize = 0
  Columns = 1
  FilletRadius = 0
  Height = 2041.87
  Length = 4100
  MakeFace = true
  Placement = pos=(15759.3,-6724.47,0) rot=(0,0,1;0rad)
  Rows = 1
FEATURE [Part::Feature] mirror165  label="Mirror of Rectangle175"
  Placement = pos=(-3623.17,-7185.78,0) rot=(0,0,1;0rad)
  shape: bbox 1801 x 800 x 2e-07 mm, 1 faces, 0 solids (baked)
FEATURE [Part::Feature] mirror166  label="Mirror of Array003"
  Placement = pos=(-3623.17,-7185.78,0) rot=(0,0,1;0rad)
  shape: bbox 1750 x 450 x 2e-07 mm, 3 faces, 0 solids (baked)
FEATURE [Part::Part2DObjectPython] Rectangle182  # Draft 2D object (typed FeaturePython)
  ChamferSize = 0
  Columns = 1
  FilletRadius = 0
  Height = 2041.87
  Length = 4100
  MakeFace = true
  Placement = pos=(21589.8,-6130.95,0) rot=(0,0,1;0rad)
  Rows = 1
FEATURE [Part::Part2DObjectPython] Rectangle187  # Draft 2D object (typed FeaturePython)
  ChamferSize = 0
  Columns = 1
  FilletRadius = 0
  Height = 6589.69
  Length = 395.411
  MakeFace = true
  Placement = pos=(14389.2,3487.32,0) rot=(0,0,1;0rad)
  Rows = 1
FEATURE [Part::Part2DObjectPython] Rectangle188  # Draft 2D object (typed FeaturePython)
  ChamferSize = 0
  Columns = 1
  FilletRadius = 0
  Height = 3306.02
  Length = 6894.85
  MakeFace = true
  Placement = pos=(14236.6,10829.6,0) rot=(0,0,-1;1.5708rad)
  Rows = 1
FEATURE [Part::Feature] mirror194  label="Mirror of DWire016"
  Placement = pos=(17329.4,-811.721,0) rot=(0,0,1;1.5708rad)
  shape: bbox 1894 x 4290 x 2e-07 mm, 1 faces, 0 solids (baked)
FEATURE [Part::Feature] mirror195  label="Mirror of Mirror of Shower009"
  Placement = pos=(11366.6,-31212.4,0) rot=(0,0,1;1.5708rad)
  shape: bbox 800 x 800 x 2e-07 mm, 2 faces, 0 solids (baked)
FEATURE [Part::Feature] mirror196  label="Mirror of Mirror of WC010"
  Placement = pos=(11366.6,-31212.4,0) rot=(0,0,1;1.5708rad)
  shape: bbox 370 x 660 x 2e-07 mm, 2 faces, 0 solids (baked)
FEATURE [Part::Feature] mirror197  label="Mirror of Sink 012"
  Placement = pos=(-10744.6,5607.34,0) rot=(0,0,1;0rad)
  shape: bbox 300 x 500 x 2e-07 mm, 3 faces, 0 solids (baked)
FEATURE [Part::Feature] mirror198  label="Mirror of Mirror of Mirror of 90cm door022"
  Placement = pos=(14430.5,-1492.71,0) rot=(0,0,1;1.5708rad)
  shape: bbox 972 x 1000 x 2e-07 mm, 5 faces, 0 solids (baked)
FEATURE [Part::Feature] mirror199  label="Mirror of DWire017"
  Placement = pos=(17329.4,-4311.05,0) rot=(0,0,1;1.5708rad)
  shape: bbox 1600 x 1602 x 2e-07 mm, 1 faces, 0 solids (baked)
FEATURE [Part::Feature] mirror200  label="Mirror of Rectangle184"
  Placement = pos=(10702.1,-9896.06,0) rot=(0,0,1;0rad)
  shape: bbox 600 x 2500 x 2e-07 mm, 1 faces, 0 solids (baked)
FEATURE [Part::Feature] mirror201  label="Mirror of Rectangle185"
  Placement = pos=(10702.1,-9896.06,0) rot=(0,0,1;0rad)
  shape: bbox 600 x 1500 x 2e-07 mm, 1 faces, 0 solids (baked)
FEATURE [Part::Feature] mirror210  label="Mirror of Sofa - 024"
  Placement = pos=(0,7619.69,0) rot=(0,0,1;0rad)
  shape: bbox 1883 x 750 x 2e-07 mm, 2 faces, 0 solids (baked)
FEATURE [Part::Feature] mirror211  label="Mirror of Rectangle187"
  Placement = pos=(0,7619.69,0) rot=(0,0,1;0rad)
  shape: bbox 603.7 x 603.7 x 2e-07 mm, 1 faces, 0 solids (baked)
FEATURE [Part::Feature] mirror212  label="Mirror of Rectangle188"
  Placement = pos=(0,7619.69,0) rot=(0,0,1;0rad)
  shape: bbox 950 x 950 x 2e-07 mm, 1 faces, 0 solids (baked)
FEATURE [Part::Feature] mirror213  label="Mirror of Mirror of Sofa - 024"
  Placement = pos=(0,7619.69,0) rot=(0,0,1;0rad)
  shape: bbox 750 x 1883 x 2e-07 mm, 2 faces, 0 solids (baked)
FEATURE [Part::Feature] mirror214  label="Mirror of Mirror of Array006"
  Placement = pos=(0,7619.69,0) rot=(0,0,1;0rad)
  shape: bbox 1750 x 450 x 2e-07 mm, 3 faces, 0 solids (baked)
FEATURE [Part::Feature] mirror215  label="Mirror of Mirror of Rectangle178"
  Placement = pos=(0,7619.69,0) rot=(0,0,1;0rad)
  shape: bbox 1801 x 800 x 2e-07 mm, 1 faces, 0 solids (baked)
FEATURE [Part::Feature] mirror216  label="Mirror of Line045"
  Placement = pos=(0,7619.69,0) rot=(0,0,1;0rad)
  shape: bbox 3001 x 0.0004885 x 2e-07 mm, 0 faces, 0 solids (baked)
FEATURE [Part::Feature] mirror217  label="Mirror of Rectangle189"
  Placement = pos=(0,7619.69,0) rot=(0,0,1;0rad)
  shape: bbox 3001 x 600 x 2e-07 mm, 1 faces, 0 solids (baked)
FEATURE [Part::Part2DObjectPython] Rectangle193  # Draft 2D object (typed FeaturePython)
  ChamferSize = 0
  Columns = 1
  FilletRadius = 0
  Height = 3306.02
  Length = 6894.85
  MakeFace = true
  Placement = pos=(10003.5,24885.3,0) rot=(0,0,-1;1.5708rad)
  Rows = 1
FEATURE [Part::Part2DObjectPython] Rectangle194  # Draft 2D object (typed FeaturePython)
  ChamferSize = 0
  Columns = 1
  FilletRadius = 0
  Height = 3000.87
  Length = 6589.69
  MakeFace = true
  Placement = pos=(10156.1,24732.7,0) rot=(0,0,-1;1.5708rad)
  Rows = 1
FEATURE [Part::Part2DObjectPython] Line048  # Draft 2D object (typed FeaturePython)
  ChamferSize = 0
  Closed = false
  End = (13157,24432.7,0)
  FilletRadius = 0
  Length = 3000.87
  MakeFace = true
  Placement = pos=(7798.54,17392.7,0) rot=(0,0,1;0rad)
  Points = (2) [(2357.57,7040,0),(5358.43,7040,0)]
  Start = (10156.1,24432.7,0)
  Subdivisions = 0
FEATURE [Part::Part2DObjectPython] Rectangle195  # Draft 2D object (typed FeaturePython)
  ChamferSize = 0
  Columns = 1
  FilletRadius = 0
  Height = 600
  Length = 3000.87
  MakeFace = true
  Placement = pos=(10156.1,24132.7,0) rot=(0,0,1;0rad)
  Rows = 1
FEATURE [Part::Feature] mirror218  label="Mirror of Rectangle190"
  Placement = pos=(672.106,12578.1,0) rot=(0,0,1;0rad)
  shape: bbox 1801 x 800 x 2e-07 mm, 1 faces, 0 solids (baked)
FEATURE [Part::Feature] mirror219  label="Mirror of Array006"
  Placement = pos=(672.106,12578.1,0) rot=(0,0,1;0rad)
  shape: bbox 1750 x 450 x 2e-07 mm, 3 faces, 0 solids (baked)
FEATURE [Part::Feature] mirror220  label="Mirror of Sofa - 025"
  Placement = pos=(18317.7,1443.14,0) rot=(0,0,1;1.5708rad)
  shape: bbox 750 x 1883 x 2e-07 mm, 2 faces, 0 solids (baked)
FEATURE [Part::Part2DObjectPython] Rectangle196  # Draft 2D object (typed FeaturePython)
  ChamferSize = 0
  Columns = 1
  FilletRadius = 0
  Height = 950
  Length = 950
  MakeFace = true
  Placement = pos=(11007.4,19358.5,0) rot=(0.707107,0.707107,0;3.14159rad)
  Rows = 1
FEATURE [Part::Part2DObjectPython] Rectangle197  # Draft 2D object (typed FeaturePython)
  ChamferSize = 0
  Columns = 1
  FilletRadius = 0
  Height = 450
  Length = 450
  MakeFace = true
  Placement = pos=(12891.9,18939.3,0) rot=(0,0,1;3.60524rad)
  Rows = 1
FEATURE [Part::Feature] Compound087  label="Sofa - 016"
  Placement = pos=(10759,16451.9,0) rot=(0,0,1;3.14159rad)
  shape: bbox 1883 x 750 x 2e-07 mm, 2 faces, 0 solids (baked)
FEATURE [Part::Feature] mirror222  label="Mirror of Rectangle191"
  Placement = pos=(-2265.75,-6269.37,0) rot=(0,0,1;0rad)
  shape: bbox 603.7 x 603.7 x 2e-07 mm, 1 faces, 0 solids (baked)
FEATURE [Part::Feature] mirror227  label="Mirror of Line046"
  Placement = pos=(0,-6294.85,0) rot=(0,0,1;0rad)
  shape: bbox 3001 x 0.0004885 x 2e-07 mm, 0 faces, 0 solids (baked)
FEATURE [Part::Feature] mirror228  label="Mirror of Rectangle193"
  Placement = pos=(0,-6294.85,0) rot=(0,0,1;0rad)
  shape: bbox 3001 x 600 x 2e-07 mm, 1 faces, 0 solids (baked)
FEATURE [Part::Feature] mirror229  label="Mirror of Mirror of Sink 013"
  Placement = pos=(-20865.6,2960.04,0) rot=(0,0,1;0rad)
  shape: bbox 500 x 300 x 2e-07 mm, 3 faces, 0 solids (baked)
FEATURE [Part::Part2DObjectPython] DWire015  # Draft 2D object (typed FeaturePython)
  ChamferSize = 0
  Closed = true
  End = (14236.6,3934.75,0)
  FilletRadius = 0
  Length = 32200.5
  MakeFace = true
  Points = (6) [(14236.6,10829.6,0),(17542.6,10829.6,0),(17542.6,7239.09,0),(23442,7239.09,0),(23442,3934.75,0),(14236.6,3934.75,0)]
  Start = (14236.6,10829.6,0)
  Subdivisions = 0
FEATURE [Part::Compound] Compound088
  Links = -> [mirror199,mirror194,mirror197,mirror195,mirror196,mirror198]
FEATURE [Part::Feature] Compound089
  Placement = pos=(6147.87,19166.4,0) rot=(0,0,-1;1.5708rad)
  shape: bbox 4290 x 1894 x 2e-07 mm, 14 faces, 0 solids (baked)
FEATURE [Part::Feature] mirror232  label="Mirror of Compound091"
  Placement = pos=(22194.4,684.266,0) rot=(0,0,1;1.5708rad)
  shape: bbox 1894 x 4290 x 2e-07 mm, 14 faces, 0 solids (baked)
FEATURE [Part::Mirroring] mirror233  label="Mirror of Mirror of Compound091"
  Base = (13264.6,10777.7,0)
  Normal = (-1,-9.0606e-08,0)
  Source = -> mirror232
FEATURE [Part::Feature] mirror264  label="Mirror of Mirror of Rectangle202"
  Placement = pos=(18066.9,25634.9,0) rot=(0,0,-1;1.5708rad)
  shape: bbox 600 x 2500 x 2e-07 mm, 1 faces, 0 solids (baked)
FEATURE [Part::Feature] mirror265  label="Mirror of Mirror of Mirror of Mirror of Mirror of Rectangle186"
  Placement = pos=(18066.9,25634.9,0) rot=(0,0,-1;1.5708rad)
  shape: bbox 600 x 1500 x 2e-07 mm, 1 faces, 0 solids (baked)
FEATURE [Part::Feature] mirror266  label="Mirror of Mirror of Mirror of Mirror of Mirror of Rectangle187"
  Placement = pos=(16697.5,25676.9,0) rot=(0,0,-1;1.5708rad)
  shape: bbox 603.7 x 603.7 x 2e-07 mm, 1 faces, 0 solids (baked)
FEATURE [Part::Feature] mirror268  label="Mirror of Mirror of Rectangle203"
  Placement = pos=(15666.9,25634.9,0) rot=(0,0,-1;1.5708rad)
  shape: bbox 3000 x 4000 x 2e-07 mm, 1 faces, 0 solids (baked)
FEATURE [Part::Feature] mirror269  label="Mirror of Mirror of Rectangle204"
  Placement = pos=(15666.9,25634.9,0) rot=(0,0,-1;1.5708rad)
  shape: bbox 3304 x 4304 x 2e-07 mm, 1 faces, 0 solids (baked)
FEATURE [Part::Feature] mirror243  label="Mirror of Mirror of Mirror of Compound094"
  Placement = pos=(13235.4,27120.8,0) rot=(0,0,-1;1.5708rad)
  shape: bbox 4290 x 1894 x 2e-07 mm, 14 faces, 0 solids (baked)
FEATURE [Part::Mirroring] mirror271  label="Mirror of DWire018"
  Base = (19642.4,15273.8,0)
  Normal = (-1,1.65871e-06,0)
  Placement = pos=(2334.65,2976.15,0) rot=(0,0,1;0rad)
FEATURE [Part::Feature] mirror272  label="Mirror of DWire019"
  Placement = pos=(37037.8,19208.6,0) rot=(0,0,1;3.14159rad)
  shape: bbox 1894 x 2542 x 2e-07 mm, 1 faces, 0 solids (baked)
FEATURE [Part::Mirroring] mirror274  label="Mirror of Mirror of Mirror of Rectangle179"
  Base = (11694.9,8840,0)
  Normal = (-1,0,0)
  Placement = pos=(8389.43,-2e-12,0) rot=(0,0,1;0rad)
FEATURE [Part::Mirroring] mirror275  label="Mirror of Mirror of Mirror of Array007"
  Base = (11694.9,8840,0)
  Normal = (-1,0,0)
  Placement = pos=(8389.43,-2e-12,0) rot=(0,0,1;0rad)
FEATURE [Part::Mirroring] mirror278  label="Mirror of Mirror of Mirror of Sofa - 025"
  Base = (11694.9,8840,0)
  Normal = (-1,0,0)
  Placement = pos=(8389.43,-2e-12,0) rot=(0,0,1;0rad)
FEATURE [Part::Mirroring] mirror279  label="Mirror of Mirror of Rectangle192"
  Base = (11694.9,8840,0)
  Normal = (-1,0,0)
  Placement = pos=(8389.43,-2e-12,0) rot=(0,0,1;0rad)
FEATURE [Part::Mirroring] mirror280  label="Mirror of Mirror of Sofa - 026"
  Base = (11694.9,8840,0)
  Normal = (-1,0,0)
  Placement = pos=(8389.43,-2e-12,0) rot=(0,0,1;0rad)
FEATURE [Part::Part2DObjectPython] Rectangle198  # Draft 2D object (typed FeaturePython)
  ChamferSize = 0
  Columns = 1
  FilletRadius = 0
  Height = 2428
  Length = 151.722
  MakeFace = true
  Placement = pos=(25716.3,4941.69,0) rot=(0,0,1;0rad)
  Rows = 1
FEATURE [Part::Part2DObjectPython] Rectangle199  # Draft 2D object (typed FeaturePython)
  ChamferSize = 0
  Columns = 1
  FilletRadius = 0
  Height = 2400.87
  Length = 153.543
  MakeFace = true
  Placement = pos=(19218.1,4968.82,0) rot=(0,0,1;0rad)
  Rows = 1
FEATURE [Part::Part2DObjectPython] Rectangle200  # Draft 2D object (typed FeaturePython)
  ChamferSize = 0
  Columns = 1
  FilletRadius = 0
  Height = 1895.83
  Length = 1894.44
  MakeFace = true
  Placement = pos=(26135.7,8709.39,0) rot=(0,0,1;1.5708rad)
  Rows = 1
FEATURE [Part::Feature] mirror290  label="Mirror of Mirror of Mirror of Mirror of Mirror of Rectangle188"
  Placement = pos=(48737.5,8570.67,0) rot=(0,0,1;3.14159rad)
  shape: bbox 603.7 x 603.7 x 2e-07 mm, 1 faces, 0 solids (baked)
FEATURE [Part::Part2DObjectPython] DWire018  # Draft 2D object (typed FeaturePython)
  ChamferSize = 0
  Closed = true
  End = (19142.6,10682.4,0)
  FilletRadius = 0
  Length = 14915.4
  MakeFace = true
  Placement = pos=(32021.8,-13249.1,0) rot=(0,0,1;1.57079rad)
  Points = (10) [(21536.9,12879.3,0),(21536.9,12732,0),(24078.6,12732,0),(24078.6,14626.5,0),(21537.9,14626.5,0),(21537.9,13851.3,0),(21684.1,13851.3,0),+3 more]
  Start = (19142.6,8287.82,0)
  Subdivisions = 0
FEATURE [Part::Feature] mirror291  label="Mirror of Mirror of 90cm door019"
  Placement = pos=(14801.4,16267.9,0) rot=(0,0,-1;1.5708rad)
  shape: bbox 972 x 1000 x 2e-07 mm, 5 faces, 0 solids (baked)
FEATURE [Part::Feature] Compound090  label="Bed-Double008"
  Placement = pos=(25097.1,6165.85,0) rot=(0,0,1;0rad)
  shape: bbox 1400 x 1900 x 2e-07 mm, 4 faces, 0 solids (baked)
FEATURE [Part::Feature] mirror293  label="Mirror of Mirror of Mirror of Compound095"
  Placement = pos=(38467.4,23575.3,0) rot=(0,0,1;3.14159rad)
  shape: bbox 1894 x 4290 x 2e-07 mm, 14 faces, 0 solids (baked)
FEATURE [Part::Feature] mirror294  label="Mirror of Mirror of Mirror of Compound096"
  Placement = pos=(31784.1,17382.4,0) rot=(0,0,1;3.14159rad)
  shape: bbox 1894 x 4290 x 2e-07 mm, 14 faces, 0 solids (baked)
FEATURE [Part::Feature] mirror301  label="Mirror of 90cm door019"
  Placement = pos=(-580.501,3145.75,0) rot=(0,0,1;0rad)
  shape: bbox 1000 x 972 x 2e-07 mm, 5 faces, 0 solids (baked)
FEATURE [Part::Part2DObjectPython] Rectangle202  # Draft 2D object (typed FeaturePython)
  ChamferSize = 0
  Columns = 1
  FilletRadius = 0
  Height = 152.175
  Length = 1352.17
  MakeFace = true
  Placement = pos=(19289.8,8092.27,0) rot=(0,0,1;1.5708rad)
  Rows = 1
FEATURE [Part::Part2DObjectPython] Rectangle203  # Draft 2D object (typed FeaturePython)
  ChamferSize = 0
  Columns = 1
  FilletRadius = 0
  Height = 3000.87
  Length = 6589.69
  MakeFace = true
  Placement = pos=(14389.2,10677,0) rot=(0,0,-1;1.5708rad)
  Rows = 1
FEATURE [Part::Part2DObjectPython] Rectangle204  # Draft 2D object (typed FeaturePython)
  ChamferSize = 0
  Columns = 1
  FilletRadius = 0
  Height = 152.174
  Length = 1748.6
  MakeFace = true
  Placement = pos=(17542.6,9444.45,0) rot=(0,0,1;0rad)
  Rows = 1
FEATURE [Part::Part2DObjectPython] Rectangle205  # Draft 2D object (typed FeaturePython)
  ChamferSize = 0
  Columns = 1
  FilletRadius = 0
  Height = 152.174
  Length = 967.049
  MakeFace = true
  Placement = pos=(18170.6,8092.27,0) rot=(0,0,1;0rad)
  Rows = 1
FEATURE [Part::Part2DObjectPython] Rectangle206  # Draft 2D object (typed FeaturePython)
  ChamferSize = 0
  Columns = 1
  FilletRadius = 0
  Height = 1895.83
  Length = 1894.44
  MakeFace = true
  Placement = pos=(22780.1,9681.22,0) rot=(0,0,1;1.5708rad)
  Rows = 1
FEATURE [Part::Feature] mirror303  label="Mirror of Mirror of 90cm door021"
  Placement = pos=(13201.4,17477.3,0) rot=(0,0,-1;1.5708rad)
  shape: bbox 972 x 1000 x 2e-07 mm, 5 faces, 0 solids (baked)
FEATURE [Part::Feature] mirror304  label="Mirror of Mirror of Mirror of 90cm door025"
  Placement = pos=(6403.77,346.164,0) rot=(0,0,1;0rad)
  shape: bbox 1000 x 972 x 2e-07 mm, 5 faces, 0 solids (baked)
FEATURE [Part::Feature] mirror307  label="Mirror of Mirror of DWire022"
  Placement = pos=(344.001,0,0) rot=(0,0,1;0rad)
  shape: bbox 1894 x 2542 x 2e-07 mm, 1 faces, 0 solids (baked)
FEATURE [Part::Feature] mirror308  label="Mirror of Mirror of Mirror of Mirror of 90cm door025"
  Placement = pos=(344.001,0,0) rot=(0,0,1;0rad)
  shape: bbox 972 x 1000 x 2e-07 mm, 5 faces, 0 solids (baked)
FEATURE [Part::Part2DObjectPython] Rectangle207  # Draft 2D object (typed FeaturePython)
  ChamferSize = 0
  Columns = 1
  FilletRadius = 0
  Height = 3306.02
  Length = 6894.85
  MakeFace = true
  Placement = pos=(29893.9,-8522.47,0) rot=(0,0,-1;1.5708rad)
  Rows = 1
FEATURE [Part::Feature] mirror309  label="Mirror of Rectangle194"
  Placement = pos=(13391.6,-25621.4,0) rot=(0,0,1;0rad)
  shape: bbox 603.7 x 603.7 x 2e-07 mm, 1 faces, 0 solids (baked)
FEATURE [Part::Feature] mirror310  label="Mirror of Line047"
  Placement = pos=(15657.4,-25646.9,0) rot=(0,0,1;0rad)
  shape: bbox 3001 x 0.0004885 x 2e-07 mm, 0 faces, 0 solids (baked)
FEATURE [Part::Feature] mirror311  label="Mirror of Rectangle195"
  Placement = pos=(15657.4,-25646.9,0) rot=(0,0,1;0rad)
  shape: bbox 3001 x 600 x 2e-07 mm, 1 faces, 0 solids (baked)
FEATURE [Part::Feature] mirror312  label="Mirror of Mirror of Sink 014"
  Placement = pos=(-5208.27,-16392,0) rot=(0,0,1;0rad)
  shape: bbox 500 x 300 x 2e-07 mm, 3 faces, 0 solids (baked)
FEATURE [Part::Feature] mirror318  label="Mirror of Mirror of Mirror of Rectangle180"
  Placement = pos=(24046.8,-19352.1,0) rot=(0,0,1;0rad)
  shape: bbox 1801 x 800 x 2e-07 mm, 1 faces, 0 solids (baked)
FEATURE [Part::Feature] mirror319  label="Mirror of Mirror of Mirror of Array008"
  Placement = pos=(24046.8,-19352.1,0) rot=(0,0,1;0rad)
  shape: bbox 1750 x 450 x 2e-07 mm, 3 faces, 0 solids (baked)
FEATURE [Part::Feature] mirror320  label="Mirror of Mirror of Mirror of Sofa - 026"
  Placement = pos=(24046.8,-19352.1,0) rot=(0,0,1;0rad)
  shape: bbox 750 x 1883 x 2e-07 mm, 2 faces, 0 solids (baked)
FEATURE [Part::Feature] mirror321  label="Mirror of Mirror of Rectangle208"
  Placement = pos=(24046.8,-19352.1,0) rot=(0,0,1;0rad)
  shape: bbox 950 x 950 x 2e-07 mm, 1 faces, 0 solids (baked)
FEATURE [Part::Feature] mirror322  label="Mirror of Mirror of Sofa - 027"
  Placement = pos=(24046.8,-19352.1,0) rot=(0,0,1;0rad)
  shape: bbox 1883 x 750 x 2e-07 mm, 2 faces, 0 solids (baked)
FEATURE [Part::Part2DObjectPython] Rectangle208  # Draft 2D object (typed FeaturePython)
  ChamferSize = 0
  Columns = 1
  FilletRadius = 0
  Height = 152.175
  Length = 1352.17
  MakeFace = true
  Placement = pos=(46066.7,-15011.1,0) rot=(0,0,1;1.5708rad)
  Rows = 1
FEATURE [Part::Part2DObjectPython] Rectangle209  # Draft 2D object (typed FeaturePython)
  ChamferSize = 0
  Columns = 1
  FilletRadius = 0
  Height = 3000.87
  Length = 6589.69
  MakeFace = true
  Placement = pos=(30046.5,-8675.04,0) rot=(0,0,-1;1.5708rad)
  Rows = 1
FEATURE [Part::Part2DObjectPython] Rectangle210  # Draft 2D object (typed FeaturePython)
  ChamferSize = 0
  Columns = 1
  FilletRadius = 0
  Height = 152.174
  Length = 1748.6
  MakeFace = true
  Placement = pos=(44319.5,-13658.9,0) rot=(0,0,1;0rad)
  Rows = 1
FEATURE [Part::Part2DObjectPython] Rectangle211  # Draft 2D object (typed FeaturePython)
  ChamferSize = 0
  Columns = 1
  FilletRadius = 0
  Height = 152.174
  Length = 967.049
  MakeFace = true
  Placement = pos=(44947.5,-15011.1,0) rot=(0,0,1;0rad)
  Rows = 1
FEATURE [Part::Feature] mirror324  label="Mirror of Mirror of 90cm door022"
  Placement = pos=(-18098.2,9646.33,0) rot=(0,0,-1;1.5708rad)
  shape: bbox 972 x 1000 x 2e-07 mm, 5 faces, 0 solids (baked)
FEATURE [Part::Feature] mirror326  label="Mirror of Mirror of DWire023"
  Placement = pos=(16001.4,-19352.1,0) rot=(0,0,1;0rad)
  shape: bbox 1894 x 2542 x 2e-07 mm, 1 faces, 0 solids (baked)
FEATURE [Part::Feature] mirror327  label="Mirror of Mirror of Mirror of Mirror of 90cm door026"
  Placement = pos=(16001.4,-19352.1,0) rot=(0,0,1;0rad)
  shape: bbox 972 x 1000 x 2e-07 mm, 5 faces, 0 solids (baked)
FEATURE [Part::Mirroring] mirror328  label="Mirror of Mirror of Mirror of Rectangle207"
  Base = (35975.8,-20834.6,0)
  Normal = (0,1,0)
FEATURE [Part::Mirroring] mirror329  label="Mirror of Mirror of Mirror of Rectangle206"
  Base = (35975.8,-20834.6,0)
  Normal = (0,1,0)
FEATURE [Part::Mirroring] mirror330  label="Mirror of Mirror of Mirror of Rectangle205"
  Base = (35975.8,-20834.6,0)
  Normal = (0,1,0)
FEATURE [Part::Mirroring] mirror331  label="Mirror of Mirror of Mirror of Mirror of Mirror of Mirror of Rectangle189"
  Base = (35975.8,-20834.6,0)
  Normal = (0,1,0)
FEATURE [Part::Mirroring] mirror332  label="Mirror of Mirror of Mirror of Mirror of Mirror of Mirror of Rectangle190"
  Base = (35975.8,-20834.6,0)
  Normal = (0,1,0)
FEATURE [Part::Mirroring] mirror333  label="Mirror of Bed-Double009"
  Base = (35975.8,-20834.6,0)
  Normal = (0,1,0)
FEATURE [Part::Mirroring] mirror334  label="Mirror of Mirror of 90cm door020"
  Base = (35975.8,-20834.6,0)
  Normal = (0,1,0)
FEATURE [Part::Mirroring] mirror342  label="Mirror of Compound092"
  Base = (43246.2,-9834.65,0)
  Normal = (-1.6e-11,1,0)
  Placement = pos=(15021.2,-253.409,0) rot=(0,0,1;0rad)
FEATURE [Part::Feature] Compound093
  Placement = pos=(25214.6,3017.83,0) rot=(0,0,1.02052;5e-06rad)
  shape: bbox 1894 x 2542 x 2e-07 mm, 6 faces, 0 solids (baked)
FEATURE [Part::Part2DObjectPython] Rectangle215  # Draft 2D object (typed FeaturePython)
  ChamferSize = 0
  Columns = 1
  FilletRadius = 0
  Height = 1749.66
  Length = 1894.44
  MakeFace = true
  Placement = pos=(37464.8,-10891.3,0) rot=(0.707107,0.707107,0;3.14159rad)
  Rows = 1
FEATURE [Part::Feature] mirror379  label="Mirror of Mirror of Mirror of Mirror of Mirror of Rectangle214"
  Placement = pos=(20221,-50812.3,0) rot=(0,0,1;1.5708rad)
  shape: bbox 4000 x 3000 x 2e-07 mm, 1 faces, 0 solids (baked)
FEATURE [Part::Feature] mirror380  label="Mirror of Mirror of Mirror of Mirror of Mirror of Rectangle215"
  Placement = pos=(20221,-50812.3,0) rot=(0,0,1;1.5708rad)
  shape: bbox 4304 x 3304 x 2e-07 mm, 1 faces, 0 solids (baked)
FEATURE [Part::Feature] mirror381  label="Mirror of Mirror of Mirror of Mirror of Mirror of Mirror of Mirror of Mirror of Rectangle195"
  Placement = pos=(20221,-53212.3,0) rot=(0,0,1;1.5708rad)
  shape: bbox 1500 x 600 x 2e-07 mm, 1 faces, 0 solids (baked)
FEATURE [Part::Feature] mirror382  label="Mirror of Mirror of Mirror of Mirror of Mirror of Mirror of Mirror of Mirror of Rectangle196"
  Placement = pos=(20190.8,-51507.8,0) rot=(0,0,1;1.5708rad)
  shape: bbox 603.7 x 603.7 x 2e-07 mm, 1 faces, 0 solids (baked)
FEATURE [Part::Feature] mirror383  label="Mirror of Mirror of Mirror of Mirror of Mirror of Rectangle216"
  Placement = pos=(20221,-53212.3,0) rot=(0,0,1;1.5708rad)
  shape: bbox 2500 x 600 x 2e-07 mm, 1 faces, 0 solids (baked)
FEATURE [Part::Feature] mirror384  label="Mirror of Mirror of Mirror of Bed-Double012"
  Placement = pos=(20221,-50112.3,0) rot=(0,0,1;1.5708rad)
  shape: bbox 1900 x 1400 x 2e-07 mm, 4 faces, 0 solids (baked)
FEATURE [Part::Feature] mirror385  label="Mirror of Compound093"
  Placement = pos=(30461.2,-71174.2,0) rot=(0,0,1;1.5708rad)
  shape: bbox 2542 x 1894 x 2e-07 mm, 6 faces, 0 solids (baked)
FEATURE [Part::Part2DObjectPython] Rectangle217  # Draft 2D object (typed FeaturePython)
  ChamferSize = 0
  Columns = 1
  FilletRadius = 0
  Height = 3152.17
  Length = 152.173
  MakeFace = true
  Placement = pos=(43331,-12411.6,0) rot=(0.707107,0.707107,0;3.14159rad)
  Rows = 1
FEATURE [Part::Part2DObjectPython] Rectangle218  # Draft 2D object (typed FeaturePython)
  ChamferSize = 0
  Columns = 1
  FilletRadius = 0
  Height = 2370.27
  Length = 152.173
  MakeFace = true
  Placement = pos=(40808.5,-12411.6,0) rot=(0.707107,0.707107,0;3.14159rad)
  Rows = 1
FEATURE [Part::Part2DObjectPython] DWire020  # Draft 2D object (typed FeaturePython)
  ChamferSize = 0
  Closed = true
  End = (41511.8,2520.35,0)
  FilletRadius = 0
  Length = 21875.6
  MakeFace = true
  Points = (11) [(40332.4,-1204.3,0),(40332.4,-1050.76,0),(38903.5,-1050.76,0),(38903.5,-2957.85,0),(41457.9,-2957.85,0),(41457.9,-1050.76,0),(41304.4,-1050.76,0),+4 more]
  Start = (40332.4,-1204.3,0)
  Subdivisions = 0
FEATURE [Part::Part2DObjectPython] DWire021  # Draft 2D object (typed FeaturePython)
  ChamferSize = 0
  Closed = true
  End = (27933.9,-16796.3,0)
  FilletRadius = 0
  Length = 14980.7
  MakeFace = true
  Placement = pos=(-11123.2,-15592,0) rot=(0,0,1;0rad)
  Points = (11) [(40332.4,-1204.3,0),(40332.4,-1050.76,0),(38903.5,-1050.76,0),(38903.5,-2957.85,0),(41457.9,-2957.85,0),(41457.9,-1050.76,0),(41304.4,-1050.76,0),+4 more]
  Start = (29209.2,-16796.3,0)
  Subdivisions = 0
FEATURE [Part::Feature] mirror394  label="Mirror of 90cm door023"
  Placement = pos=(25234.7,3073.98,0) rot=(0,0,-1;1.5708rad)
  shape: bbox 972 x 1000 x 2e-07 mm, 5 faces, 0 solids (baked)
FEATURE [Part::Part2DObjectPython] DWire022  # Draft 2D object (typed FeaturePython)
  ChamferSize = 0
  Closed = true
  End = (33047.4,-13663.8,0)
  FilletRadius = 0
  Length = 35087.2
  MakeFace = true
  Points = (8) [(33047.4,-8675.04,0),(30046.5,-8675.04,0),(30046.5,-15264.7,0),(39601.8,-15264.7,0),(39601.8,-12265.1,0),(35601.8,-12265.1,0),(35601.8,-13663.8,0),+1 more]
  Start = (33047.4,-8675.04,0)
  Subdivisions = 0
FEATURE [Part::Part2DObjectPython] Rectangle219  # Draft 2D object (typed FeaturePython)
  ChamferSize = 0
  Columns = 1
  FilletRadius = 0
  Height = 3000
  Length = 3000
  MakeFace = true
  Placement = pos=(42093.4,-10342.2,0) rot=(0.707107,0.707107,0;3.14159rad)
  Rows = 1
FEATURE [Part::Part2DObjectPython] Rectangle220  # Draft 2D object (typed FeaturePython)
  ChamferSize = 0
  Columns = 1
  FilletRadius = 0
  Height = 3000
  Length = 3000
  MakeFace = true
  Placement = pos=(33047.4,-11522.5,0) rot=(0.707107,0.707107,0;3.14159rad)
  Rows = 1
FEATURE [Part::Part2DObjectPython] DWire023  # Draft 2D object (typed FeaturePython)
  ChamferSize = 0
  Closed = true
  End = (41665.5,-10092,0)
  FilletRadius = 0
  Length = 14474.8
  MakeFace = true
  Placement = pos=(6215.93,3418.23,0) rot=(0,0,1;0rad)
  Points = (6) [(35449.6,-12113,0),(34474.9,-12113,0),(34474.9,-8522.46,0),(33200,-8522.47,0),(33200,-13510.2,0),(35449.6,-13510.2,0)]
  Start = (41665.5,-8694.73,0)
  Subdivisions = 0
FEATURE [Part::Mirroring] mirror395  label="Mirror of Rectangle221"
  Base = (34474.9,-10317.7,0)
  Normal = (0,1,0)
  Placement = pos=(6215.93,2020.97,0) rot=(0,0,1;0rad)
FEATURE [Part::Feature] mirror396  label="Mirror of Mirror of 90cm door023"
  Placement = pos=(28858.8,-4832.33,0) rot=(0,0,-1;1.5708rad)
  shape: bbox 972 x 1000 x 2e-07 mm, 5 faces, 0 solids (baked)
FEATURE [Part::Feature] mirror397  label="Mirror of Compound094"
  Placement = pos=(33776.3,-71661.5,0) rot=(0,0,1;1.5708rad)
  shape: bbox 2542 x 1894 x 2e-07 mm, 6 faces, 0 solids (baked)
FEATURE [Part::Feature] mirror411  label="Mirror of Mirror of Mirror of Sofa - 028"
  Placement = pos=(-25458.1,26638.9,0) rot=(0,0,1;0rad)
  shape: bbox 1883 x 750 x 2e-07 mm, 2 faces, 0 solids (baked)
FEATURE [Part::Feature] mirror412  label="Mirror of Mirror of Rectangle209"
  Placement = pos=(-25458.1,26638.9,0) rot=(0,0,1;0rad)
  shape: bbox 603.7 x 603.7 x 2e-07 mm, 1 faces, 0 solids (baked)
FEATURE [Part::Feature] mirror413  label="Mirror of Mirror of Mirror of Rectangle209"
  Placement = pos=(-25458.1,26638.9,0) rot=(0,0,1;0rad)
  shape: bbox 950 x 950 x 2e-07 mm, 1 faces, 0 solids (baked)
FEATURE [Part::Feature] mirror414  label="Mirror of Mirror of Mirror of Mirror of Sofa - 027"
  Placement = pos=(-25458.1,26638.9,0) rot=(0,0,1;0rad)
  shape: bbox 750 x 1883 x 2e-07 mm, 2 faces, 0 solids (baked)
FEATURE [Part::Feature] mirror417  label="Mirror of Mirror of Mirror of Mirror of Array013"
  Placement = pos=(-25458.1,26638.9,0) rot=(0,0,1;0rad)
  shape: bbox 1750 x 450 x 2e-07 mm, 3 faces, 0 solids (baked)
FEATURE [Part::Feature] mirror418  label="Mirror of Mirror of Mirror of Mirror of Rectangle181"
  Placement = pos=(-25458.1,26638.9,0) rot=(0,0,1;0rad)
  shape: bbox 1801 x 800 x 2e-07 mm, 1 faces, 0 solids (baked)
FEATURE [Part::Feature] mirror419  label="Mirror of Rectangle222"
  Placement = pos=(-25458.1,26638.9,0) rot=(0,0,1;0rad)
  shape: bbox 3306 x 6895 x 2e-07 mm, 1 faces, 0 solids (baked)
FEATURE [Part::Feature] mirror420  label="Mirror of Rectangle223"
  Placement = pos=(-25458.1,26638.9,0) rot=(0,0,1;0rad)
  shape: bbox 3001 x 6590 x 2e-07 mm, 1 faces, 0 solids (baked)
FEATURE [Part::Feature] mirror421  label="Mirror of Mirror of Line048"
  Placement = pos=(-25458.1,26638.9,0) rot=(0,0,1;0rad)
  shape: bbox 3001 x 0.0004885 x 2e-07 mm, 0 faces, 0 solids (baked)
FEATURE [Part::Feature] mirror422  label="Mirror of Mirror of Rectangle210"
  Placement = pos=(-25458.1,26638.9,0) rot=(0,0,1;0rad)
  shape: bbox 3001 x 600 x 2e-07 mm, 1 faces, 0 solids (baked)
FEATURE [Part::Feature] mirror423  label="Mirror of Mirror of Mirror of Sink 015"
  Placement = pos=(-25458.1,26638.9,0) rot=(0,0,1;0rad)
  shape: bbox 500 x 300 x 2e-07 mm, 3 faces, 0 solids (baked)
FEATURE [Part::Feature] mirror437  label="Mirror of Mirror of Rectangle224"
  Placement = pos=(-9508.97,412.332,0) rot=(0,0,1;0rad)
  shape: bbox 3306 x 6895 x 2e-07 mm, 1 faces, 0 solids (baked)
FEATURE [Part::Feature] mirror438  label="Mirror of Mirror of Rectangle225"
  Placement = pos=(-25444.8,26187,0) rot=(0,0,1;0rad)
  shape: bbox 3001 x 6590 x 2e-07 mm, 1 faces, 0 solids (baked)
FEATURE [Part::Feature] mirror439  label="Mirror of Mirror of Mirror of Line049"
  Placement = pos=(15640.9,-60779.8,0) rot=(0,0,1;1.5708rad)
  shape: bbox 0.0004885 x 3001 x 2e-07 mm, 0 faces, 0 solids (baked)
FEATURE [Part::Feature] mirror440  label="Mirror of Mirror of Mirror of Rectangle212"
  Placement = pos=(15640.9,-60779.8,0) rot=(0,0,1;1.5708rad)
  shape: bbox 600 x 3001 x 2e-07 mm, 1 faces, 0 solids (baked)
FEATURE [Part::Feature] mirror441  label="Mirror of Mirror of Mirror of Mirror of Sink 016"
  Placement = pos=(15640.9,-60779.8,0) rot=(0,0,1;1.5708rad)
  shape: bbox 300 x 500 x 2e-07 mm, 3 faces, 0 solids (baked)
FEATURE [Part::Feature] mirror442  label="Mirror of Mirror of Mirror of Mirror of Mirror of Rectangle217"
  Placement = pos=(15640.9,-60779.8,0) rot=(0,0,1;1.5708rad)
  shape: bbox 800 x 1801 x 2e-07 mm, 1 faces, 0 solids (baked)
FEATURE [Part::Feature] mirror443  label="Mirror of Mirror of Mirror of Mirror of Mirror of Array016"
  Placement = pos=(15640.9,-60779.8,0) rot=(0,0,1;1.5708rad)
  shape: bbox 450 x 1750 x 2e-07 mm, 3 faces, 0 solids (baked)
FEATURE [Part::Feature] Compound094  label="Door-90cm009"
  Placement = pos=(35357.4,790.606,0) rot=(0,0,1;1.5708rad)
  shape: bbox 1000 x 972 x 2e-07 mm, 5 faces, 0 solids (baked)
FEATURE [Part::Feature] mirror448  label="Mirror of DWire021"
  Placement = pos=(-1770.22,11655.6,0) rot=(0,0,1;0rad)
  shape: bbox 2554 x 1907 x 2e-07 mm, 1 faces, 0 solids (baked)
FEATURE [Part::Part2DObjectPython] DWire024  # Draft 2D object (typed FeaturePython)
  ChamferSize = 0
  Closed = true
  End = (33911.6,4952.69,0)
  FilletRadius = 0
  Length = 6404.88
  MakeFace = true
  Placement = pos=(47762.8,-15582.8,0) rot=(0,0,1;1.5708rad)
  Points = (6) [(21537.9,13851.3,0),(21537.9,14479.3,0),(19935.5,14479.3,0),(19935.5,12879.3,0),(20535.5,12879.3,0),(20535.5,13851.3,0)]
  Start = (33911.6,5955.13,0)
  Subdivisions = 0
FEATURE [Part::Part2DObjectPython] Rectangle222  # Draft 2D object (typed FeaturePython)
  ChamferSize = 0
  Columns = 1
  FilletRadius = 0
  Height = 1602.44
  Length = 153.543
  MakeFace = true
  Placement = pos=(39687.7,8544.26,0) rot=(0.707107,0.707107,0;3.14159rad)
  Rows = 1
FEATURE [Part::Part2DObjectPython] Rectangle223  # Draft 2D object (typed FeaturePython)
  ChamferSize = 0
  Columns = 1
  FilletRadius = 0
  Height = 1602.44
  Length = 153.543
  MakeFace = true
  Placement = pos=(39687.7,6790.71,0) rot=(0.707107,0.707107,0;3.14159rad)
  Rows = 1
FEATURE [Part::Feature] mirror449  label="Mirror of Mirror of Mirror of 90cm door026"
  Placement = pos=(39224.7,-1877.68,0) rot=(0,0,1;1.5708rad)
  shape: bbox 972 x 1000 x 2e-07 mm, 5 faces, 0 solids (baked)
FEATURE [Part::Feature] mirror450  label="Mirror of Mirror of Mirror of Mirror of Mirror of Rectangle218"
  Placement = pos=(74819.5,-11023.5,0) rot=(0,0,1;3.14159rad)
  shape: bbox 3304 x 4304 x 2e-07 mm, 1 faces, 0 solids (baked)
FEATURE [Part::Feature] mirror452  label="Mirror of Mirror of Mirror of Mirror of Mirror of Mirror of Mirror of Mirror of Rectangle197"
  Placement = pos=(77219.5,-11023.5,0) rot=(0,0,1;3.14159rad)
  shape: bbox 600 x 1500 x 2e-07 mm, 1 faces, 0 solids (baked)
FEATURE [Part::Feature] mirror453  label="Mirror of Mirror of Mirror of Mirror of Mirror of Mirror of Mirror of Mirror of Rectangle198"
  Placement = pos=(75514.9,-11053.7,0) rot=(0,0,1;3.14159rad)
  shape: bbox 603.7 x 603.7 x 2e-07 mm, 1 faces, 0 solids (baked)
FEATURE [Part::Part2DObjectPython] Rectangle224  # Draft 2D object (typed FeaturePython)
  ChamferSize = 0
  Columns = 1
  FilletRadius = 0
  Height = 3999.6
  Length = 3000
  MakeFace = true
  Placement = pos=(39872.3,1955.53,0) rot=(0,1,0;3.14159rad)
  Rows = 1
FEATURE [Part::Feature] mirror455  label="Mirror of Mirror of Mirror of Mirror of Mirror of Sofa - 029"
  Placement = pos=(-69120.9,42912.8,0) rot=(0,0,1;0rad)
  shape: bbox 750 x 1883 x 2e-07 mm, 2 faces, 0 solids (baked)
FEATURE [Part::Feature] mirror456  label="Mirror of Mirror of Mirror of Rectangle214"
  Placement = pos=(-69120.9,42912.8,0) rot=(0,0,1;0rad)
  shape: bbox 603.7 x 603.7 x 2e-07 mm, 1 faces, 0 solids (baked)
FEATURE [Part::Feature] mirror457  label="Mirror of Mirror of Mirror of Mirror of Sofa - 030"
  Placement = pos=(-69120.9,42912.8,0) rot=(0,0,1;0rad)
  shape: bbox 1883 x 750 x 2e-07 mm, 2 faces, 0 solids (baked)
FEATURE [Part::Feature] mirror458  label="Mirror of Mirror of Mirror of Mirror of Rectangle211"
  Placement = pos=(-69120.9,42912.8,0) rot=(0,0,1;0rad)
  shape: bbox 950 x 950 x 2e-07 mm, 1 faces, 0 solids (baked)
FEATURE [Part::Feature] Compound095  label="Sofa - 017"
  Placement = pos=(35210.8,4416.62,0) rot=(0,0,1;3.14159rad)
  shape: bbox 1400 x 750 x 2e-07 mm, 2 faces, 0 solids (baked)
FEATURE [Part::Part2DObjectPython] Rectangle225  # Draft 2D object (typed FeaturePython)
  ChamferSize = 0
  Columns = 1
  FilletRadius = 0
  Height = 1500
  Length = 6894.85
  MakeFace = true
  Placement = pos=(40024.9,9261.15,0) rot=(0,1,0;3.14159rad)
  Rows = 1
FEATURE [Part::Part2DObjectPython] Rectangle228  # Draft 2D object (typed FeaturePython)
  ChamferSize = 0
  Columns = 1
  FilletRadius = 0
  Height = 1683.01
  Length = 153.543
  MakeFace = true
  Placement = pos=(38562.2,5107.7,0) rot=(0,1,0;3.14159rad)
  Rows = 1
FEATURE [Part::Part2DObjectPython] Rectangle229  # Draft 2D object (typed FeaturePython)
  ChamferSize = 0
  Columns = 1
  FilletRadius = 0
  Height = 3000.4
  Length = 600.001
  MakeFace = true
  Placement = pos=(39872.7,5355.13,0) rot=(0,0,1;1.5708rad)
  Rows = 1
FEATURE [Part::Feature] mirror464  label="Mirror of Door-90cm013"
  Placement = pos=(17841.9,-50114.8,0) rot=(0,0,1;1.5708rad)
  shape: bbox 1000 x 972 x 2e-07 mm, 5 faces, 0 solids (baked)
FEATURE [Part::Feature] mirror466  label="Mirror of Mirror of Mirror of Mirror of 90cm door028"
  Placement = pos=(17889.7,-54198.8,0) rot=(0,0,1;1.5708rad)
  shape: bbox 972 x 1000 x 2e-07 mm, 5 faces, 0 solids (baked)
FEATURE [Part::Part2DObjectPython] DWire025  # Draft 2D object (typed FeaturePython)
  ChamferSize = 0
  Closed = true
  End = (36720.1,4383.13,0)
  FilletRadius = 0
  Length = 77743.7
  MakeFace = true
  Placement = pos=(16053.2,-51270.8,0) rot=(0,0,1;1.5708rad)
  Points = (34) [(53074.2,-20666.9,0),(53074.2,-23971.3,0),(60532,-23971.3,0),(60532,-17076.8,0),(53069.1,-17076.8,0),(53069.1,-18983.9,0),(54344.4,-18983.9,0),+27 more]
  Start = (36720.1,1803.36,0)
  Subdivisions = 0
FEATURE [Part::Part2DObjectPython] DWire026  # Draft 2D object (typed FeaturePython)
  ChamferSize = 0
  Closed = true
  End = (34883.6,1951.82,0)
  FilletRadius = 0
  Length = 30034.2
  MakeFace = true
  Placement = pos=(16053.2,-51270.8,0) rot=(0,0,1;1.5708rad)
  Points = (8) [(53222.6,-17230.4,0),(60379.4,-17230.4,0),(60379.4,-23819.1,0),(53226.3,-23819.1,0),(53226.3,-20819.1,0),(54498,-20819.1,0),(54498,-18830.4,0),+1 more]
  Start = (33283.6,1951.82,0)
  Subdivisions = 0
FEATURE [Part::Feature] mirror467  label="Mirror of 90cm door024"
  Placement = pos=(44034.1,-23605.6,0) rot=(0,0,1;1.5708rad)
  shape: bbox 972 x 1000 x 2e-07 mm, 5 faces, 0 solids (baked)
FEATURE [Part::Feature] mirror468  label="Mirror of Mirror of Mirror of Mirror of 90cm door029"
  Placement = pos=(44034.1,-23605.6,0) rot=(0,0,1;1.5708rad)
  shape: bbox 972 x 1000 x 2e-07 mm, 5 faces, 0 solids (baked)
FEATURE [Part::Feature] mirror469  label="Mirror of 90cm door025"
  Placement = pos=(40592.5,-23605.6,0) rot=(0,0,1;1.5708rad)
  shape: bbox 972 x 1000 x 2e-07 mm, 5 faces, 0 solids (baked)
FEATURE [Part::Feature] mirror470  label="Mirror of WC006"
  Placement = pos=(47128.3,9095.29,0) rot=(0,0,-1;1.5708rad)
  shape: bbox 660 x 370 x 2e-07 mm, 2 faces, 0 solids (baked)
FEATURE [Part::Feature] mirror471  label="Mirror of Sink 013"
  Placement = pos=(47128.3,9171.4,0) rot=(0,0,-1;1.5708rad)
  shape: bbox 500 x 300 x 2e-07 mm, 3 faces, 0 solids (baked)
FEATURE [Part::Feature] mirror472  label="Mirror of Shower006"
  Placement = pos=(47128.3,9021.4,0) rot=(0,0,-1;1.5708rad)
  shape: bbox 800 x 800 x 2e-07 mm, 2 faces, 0 solids (baked)
FEATURE [Part::Part2DObjectPython] Rectangle230  # Draft 2D object (typed FeaturePython)
  ChamferSize = 0
  Columns = 1
  FilletRadius = 0
  Height = 2554.41
  Length = 1907.09
  MakeFace = false
  Placement = pos=(45460.2,-9909.04,0) rot=(0,0,-1;1.5708rad)
  Rows = 1
FEATURE [Part::Part2DObjectPython] Rectangle231  # Draft 2D object (typed FeaturePython)
  ChamferSize = 0
  Columns = 1
  FilletRadius = 0
  Height = 2247.32
  Length = 1600
  MakeFace = false
  Placement = pos=(45613.7,-10062.6,0) rot=(0,0,-1;1.5708rad)
  Rows = 1
  Support = -> [Compound030]
FEATURE [Part::Feature] mirror473  label="Mirror of Mirror of WC011"
  Placement = pos=(14060.3,-12866.9,0) rot=(0,0,1;0rad)
  shape: bbox 660 x 370 x 2e-07 mm, 2 faces, 0 solids (baked)
FEATURE [Part::Feature] mirror474  label="Mirror of Mirror of Sink 015"
  Placement = pos=(14060.3,-12866.9,0) rot=(0,0,1;0rad)
  shape: bbox 500 x 300 x 2e-07 mm, 3 faces, 0 solids (baked)
FEATURE [Part::Feature] mirror475  label="Mirror of Mirror of Shower010"
  Placement = pos=(14060.3,-12866.9,0) rot=(0,0,1;0rad)
  shape: bbox 800 x 800 x 2e-07 mm, 2 faces, 0 solids (baked)
FEATURE [Part::Feature] mirror476  label="Mirror of Rectangle224"
  Placement = pos=(14060.3,-12866.9,0) rot=(0,0,1;0rad)
  shape: bbox 2554 x 1907 x 2e-07 mm, 0 faces, 0 solids (baked)
FEATURE [Part::Feature] mirror477  label="Mirror of Rectangle225"
  Placement = pos=(14060.3,-12866.9,0) rot=(0,0,1;0rad)
  shape: bbox 2247 x 1600 x 2e-07 mm, 0 faces, 0 solids (baked)
FEATURE [Part::Feature] mirror478  label="Mirror of 90cm door026"
  Placement = pos=(46666.3,9880.71,0) rot=(0,0,-1;1.5708rad)
  shape: bbox 972 x 1000 x 2e-07 mm, 5 faces, 0 solids (baked)
FEATURE [Part::Feature] mirror479  label="Mirror of Mirror of Mirror of Rectangle215"
  Placement = pos=(31502.4,-23938.8,0) rot=(0,0,1;1.5708rad)
  shape: bbox 950 x 950 x 2e-07 mm, 1 faces, 0 solids (baked)
FEATURE [Part::Feature] mirror480  label="Mirror of Mirror of Mirror of Sofa - 029"
  Placement = pos=(31502.4,-23938.8,0) rot=(0,0,1;1.5708rad)
  shape: bbox 750 x 1883 x 2e-07 mm, 2 faces, 0 solids (baked)
FEATURE [Part::Feature] mirror481  label="Mirror of Mirror of Rectangle226"
  Placement = pos=(31502.4,-23938.8,0) rot=(0,0,1;1.5708rad)
  shape: bbox 603.7 x 603.7 x 2e-07 mm, 1 faces, 0 solids (baked)
FEATURE [Part::Feature] mirror454  label="Mirror of Mirror of Mirror of Bed-Double013"
  Placement = pos=(22893.3,-31841.6,0) rot=(0,0,1;1.5708rad)
  shape: bbox 1900 x 1400 x 2e-07 mm, 4 faces, 0 solids (baked)
FEATURE [Part::Feature] mirror482  label="Mirror of WC007"
  Placement = pos=(14125.7,3466.44,0) rot=(0,0,1;0rad)
  shape: bbox 370 x 660 x 2e-07 mm, 2 faces, 0 solids (baked)
FEATURE [Part::Feature] mirror483  label="Mirror of Shower007"
  Placement = pos=(14199.6,3466.38,0) rot=(0,0,1;0rad)
  shape: bbox 800 x 800 x 2e-07 mm, 2 faces, 0 solids (baked)
FEATURE [Part::Feature] mirror484  label="Mirror of Sink 014"
  Placement = pos=(14049.6,3466.38,0) rot=(0,0,1;0rad)
  shape: bbox 300 x 500 x 2e-07 mm, 3 faces, 0 solids (baked)
FEATURE [App::DocumentObjectGroup] Group010  label="All Other"
  Group = -> [Rectangle016,Rectangle022,Rectangle023,Rectangle024,Face,Rectangle025,Line001,Line002,Block,Rectangle026,Circle,Compound003,Rectangle027,Face004,Compound004,Group003,Rectangle028,mirror008,Construction,Compound021,Compound011,Compound022,Compound008,mirror009,Shell003,mirror013,Compound034,Rectangle072,mirror030,Compound048,Compound049,Line016,Rectangle078,Line017,Compound,Rectangle082,Group007,+198 more]
FEATURE [App::DocumentObjectGroup] Group011  label="Assets001"
  Group = -> [Line048,Rectangle195,Rectangle194,Rectangle193,mirror218,mirror219,mirror220,Rectangle196,Compound087,Rectangle197,Compound089,mirror326,mirror327]
FEATURE [App::FeaturePython] Dimension006  # Draft dimension (typed FeaturePython)
  Diameter = false
  Dimline = (17764.5,9323.23,0)
  Direction = (0,0,0)
  Distance = 11555.3
  End = (29019.8,8123.23,0)
  Normal = (0,0,1)
  Start = (17464.5,8123.23,0)
FEATURE [App::FeaturePython] Dimension007  # Draft dimension (typed FeaturePython)
  Diameter = false
  Dimline = (18064.5,8723.23,0)
  Direction = (0,0,0)
  Distance = 1753.54
  End = (19218.1,8123.23,0)
  Normal = (0,0,1)
  Start = (17464.5,8123.23,0)
FEATURE [App::FeaturePython] Dimension008  # Draft dimension (typed FeaturePython)
  Diameter = false
  Dimline = (19218.1,8723.23,0)
  Direction = (0,0,0)
  Distance = 6651.82
  End = (25869.9,8123.23,0)
  Normal = (0,0,1)
  Start = (19218.1,8123.23,0)
FEATURE [App::FeaturePython] Dimension009  # Draft dimension (typed FeaturePython)
  Diameter = false
  Dimline = (25869.9,8723.23,0)
  Direction = (0,0,0)
  Distance = 3149.9
  End = (29019.8,8123.23,0)
  Normal = (0,0,1)
  Start = (25869.9,8123.23,0)
FEATURE [App::FeaturePython] Dimension010  # Draft dimension (typed FeaturePython)
  Diameter = false
  Dimline = (16264.5,8723.23,0)
  Direction = (0,0,0)
  Distance = 4907.09
  End = (17464.5,3216.15,0)
  Normal = (0,0,1)
  Start = (17464.5,8123.23,0)
FEATURE [App::FeaturePython] Dimension011  # Draft dimension (typed FeaturePython)
  Diameter = false
  Dimline = (16864.5,8723.23,0)
  Direction = (0,0,0)
  Distance = 4307.09
  End = (17464.5,7523.23,0)
  Normal = (0,0,1)
  Start = (17464.5,3216.15,0)
FEATURE [App::FeaturePython] Dimension012  # Draft dimension (typed FeaturePython)
  Diameter = false
  Dimline = (16864.5,7523.23,0)
  Direction = (0,0,0)
  Distance = 600
  End = (17464.5,8123.23,0)
  Normal = (0,0,1)
  Start = (17464.5,7523.23,0)
FEATURE [App::FeaturePython] Dimension013  # Draft dimension (typed FeaturePython)
  Diameter = false
  Dimline = (17464.5,2016.15,0)
  Direction = (0,0,0)
  Distance = 953.544
  End = (18418.1,3216.15,0)
  Normal = (0,0,1)
  Start = (17464.5,3216.15,0)
FEATURE [App::FeaturePython] Dimension014  # Draft dimension (typed FeaturePython)
  Diameter = false
  Dimline = (18064.5,2016.15,0)
  Direction = (0,0,0)
  Distance = 8950
  End = (27368.1,1717.4,0)
  Normal = (0,0,1)
  Start = (18418.1,1717.4,0)
FEATURE [App::FeaturePython] Dimension015  # Draft dimension (typed FeaturePython)
  Diameter = false
  Dimline = (18064.5,2016.15,0)
  Direction = (0,0,0)
  Distance = 1651.72
  End = (29019.8,3217.97,0)
  Normal = (0,0,1)
  Start = (27368.1,3217.97,0)
FEATURE [App::FeaturePython] Dimension016  # Draft dimension (typed FeaturePython)
  Diameter = false
  Dimline = (17764.5,2616.15,0)
  Direction = (0,0,0)
  Distance = 6344.73
  End = (25716.3,3217.97,0)
  Normal = (0,0,1)
  Start = (19371.6,3216.15,0)
FEATURE [App::FeaturePython] Dimension017  # Draft dimension (typed FeaturePython)
  Diameter = false
  Dimline = (17764.5,2616.15,0)
  Direction = (0,0,0)
  Distance = 3303.44
  End = (29019.8,3217.97,0)
  Normal = (0,0,1)
  Start = (25716.3,3217.97,0)
FEATURE [App::FeaturePython] Dimension018  # Draft dimension (typed FeaturePython)
  Diameter = false
  Dimline = (17764.5,2616.15,0)
  Direction = (0,0,0)
  Distance = 1907.09
  End = (19371.6,3216.15,0)
  Normal = (0,0,1)
  Start = (17464.5,3216.15,0)
FEATURE [App::FeaturePython] Dimension019  # Draft dimension (typed FeaturePython)
  Diameter = false
  Dimline = (18861.7,6288.88,0)
  Direction = (0,0,0)
  Distance = 1600
  End = (19218.1,4968.82,0)
  Normal = (0,0,1)
  Start = (17618.1,4968.82,0)
FEATURE [App::FeaturePython] Dimension020  # Draft dimension (typed FeaturePython)
  Diameter = false
  Dimline = (19218.1,6288.88,0)
  Direction = (0,0,0)
  Distance = 1805.46
  End = (21177.1,7369.69,0)
  Normal = (0,0,1)
  Start = (19371.6,7369.69,0)
FEATURE [App::FeaturePython] Dimension021  # Draft dimension (typed FeaturePython)
  Diameter = false
  Dimline = (21177.1,6288.88,0)
  Direction = (0,0,0)
  Distance = 800
  End = (21977.1,7369.69,0)
  Normal = (0,0,1)
  Start = (21177.1,7369.69,0)
FEATURE [App::FeaturePython] Dimension022  # Draft dimension (typed FeaturePython)
  Diameter = false
  Dimline = (19782.2,7507.1,0)
  Direction = (0,0,0)
  Distance = 600
  End = (19371.6,7369.69,0)
  Normal = (0,0,1)
  Start = (19371.6,7969.69,0)
FEATURE [App::FeaturePython] Dimension023  # Draft dimension (typed FeaturePython)
  Diameter = false
  Dimline = (19782.2,7369.69,0)
  Direction = (0,0,0)
  Distance = 1800.87
  End = (21177.1,5568.83,0)
  Normal = (0,0,1)
  Start = (21177.1,7369.69,0)
FEATURE [App::DocumentObjectGroup] Group012  label="Dims Plan 1"
  Group = -> [Dimension006,Dimension007,Dimension008,Dimension009,Dimension010,Dimension011,Dimension012,Dimension013,Dimension014,Dimension015,Dimension016,Dimension017,Dimension018,Dimension019,Dimension020,Dimension021,Dimension022,Dimension023]
FEATURE [App::DocumentObjectGroup] Group008  label="Plan 1"
  Group = -> [Rectangle150,mirror136,mirror137,mirror138,Compound075,Rectangle151,Line037,Line039,Compound076,Line040,Rectangle152,Rectangle153,Array,DWire008,DWire009,Compound077,Rectangle157,Rectangle158,Rectangle161,Rectangle163,Rectangle166,Rectangle167,Clone002,Compound078,mirror139,Rectangle168,Rectangle169,DWire010,DWire011,mirror145,mirror146,mirror147,mirror148,DWire012,mirror200,mirror201,+4 more]
FEATURE [App::FeaturePython] Dimension027  # Draft dimension (typed FeaturePython)
  Diameter = false
  Dimline = (39686.8,987.728,0)
  Direction = (0,0,0)
  Distance = 3304.35
  End = (40024.5,1803.36,0)
  Normal = (0,0,1)
  Start = (36720.1,1803.36,0)
FEATURE [App::FeaturePython] Dimension028  # Draft dimension (typed FeaturePython)
  Diameter = false
  Dimline = (36720.1,987.728,0)
  Direction = (0,0,0)
  Distance = 1907.09
  End = (35037.1,1798.28,0)
  Normal = (0,0,1)
  Start = (33130,1798.28,0)
FEATURE [App::FeaturePython] Dimension029  # Draft dimension (typed FeaturePython)
  Diameter = false
  Dimline = (33130,9861.15,0)
  Direction = (0,0,0)
  Distance = 6894.44
  End = (40024.5,9261.15,0)
  Normal = (0,0,1)
  Start = (33130,9261.15,0)
FEATURE [App::FeaturePython] Dimension030  # Draft dimension (typed FeaturePython)
  Diameter = false
  Dimline = (32530,9561.15,0)
  Direction = (0,0,0)
  Distance = 7462.87
  End = (33130,9261.15,0)
  Normal = (0,0,1)
  Start = (33130,1798.28,0)
FEATURE [App::FeaturePython] Dimension031  # Draft dimension (typed FeaturePython)
  Diameter = false
  Dimline = (35037.1,987.728,0)
  Direction = (0,0,0)
  Distance = 1683.01
  End = (36720.1,3073.6,0)
  Normal = (0,0,1)
  Start = (35037.1,3073.6,0)
FEATURE [Part::Part2DObjectPython] Rectangle242  # Draft 2D object (typed FeaturePython)
  ChamferSize = 0
  Columns = 1
  FilletRadius = 0
  Height = 1683.01
  Length = 1270.24
  MakeFace = true
  Placement = pos=(36720.1,1803.36,0) rot=(0,0,1;1.5708rad)
  Rows = 1
FEATURE [App::FeaturePython] Dimension032  # Draft dimension (typed FeaturePython)
  Diameter = false
  Dimline = (34338.7,8490.94,0)
  Direction = (0,0,0)
  Distance = 600
  End = (33882.6,9108.57,0)
  Normal = (0,0,1)
  Start = (33282.6,9108.57,0)
FEATURE [App::FeaturePython] Dimension033  # Draft dimension (typed FeaturePython)
  Diameter = false
  Dimline = (33882.6,8490.94,0)
  Direction = (0,0,0)
  Distance = 1500.05
  End = (35382.7,9108.57,0)
  Normal = (0,0,1)
  Start = (33882.6,9108.57,0)
FEATURE [App::FeaturePython] Dimension034  # Draft dimension (typed FeaturePython)
  Diameter = false
  Dimline = (35382.7,8490.94,0)
  Direction = (0,0,0)
  Distance = 800
  End = (36182.7,9108.57,0)
  Normal = (0,0,1)
  Start = (35382.7,9108.57,0)
FEATURE [App::FeaturePython] Dimension035  # Draft dimension (typed FeaturePython)
  Diameter = false
  Dimline = (35177.9,7814.4,0)
  Direction = (0,0,0)
  Distance = 1800.87
  End = (35382.7,9108.57,0)
  Normal = (0,0,1)
  Start = (35382.7,7307.7,0)
FEATURE [App::FeaturePython] Dimension036  # Draft dimension (typed FeaturePython)
  Diameter = false
  Dimline = (35177.9,7307.7,0)
  Direction = (0,0,0)
  Distance = 1200
  End = (35382.7,6107.7,0)
  Normal = (0,0,1)
  Start = (35382.7,7307.7,0)
FEATURE [App::FeaturePython] Dimension037  # Draft dimension (typed FeaturePython)
  Diameter = false
  Dimline = (34471.3,5382.23,0)
  Direction = (0,0,0)
  Distance = 1600
  End = (34883.6,4352.69,0)
  Normal = (0,0,1)
  Start = (33283.6,4352.69,0)
FEATURE [App::FeaturePython] Dimension038  # Draft dimension (typed FeaturePython)
  Diameter = false
  Dimline = (33683.3,3003,0)
  Direction = (0,0,0)
  Distance = 2247.32
  End = (33283.6,1951.82,0)
  Normal = (0,0,1)
  Start = (33283.6,4199.14,0)
FEATURE [App::FeaturePython] Dimension039  # Draft dimension (typed FeaturePython)
  Diameter = false
  Dimline = (37244.7,3030.84,0)
  Direction = (0,0,0)
  Distance = 3999.6
  End = (36872.3,1955.53,0)
  Normal = (0,0,1)
  Start = (36872.3,5955.13,0)
FEATURE [App::FeaturePython] Dimension040  # Draft dimension (typed FeaturePython)
  Diameter = false
  Dimline = (37466.9,2202.09,0)
  Direction = (0,0,0)
  Distance = 3000
  End = (39872.3,1955.53,0)
  Normal = (0,0,1)
  Start = (36872.3,1955.53,0)
FEATURE [App::DocumentObjectGroup] Group013  label="Dim Plan 2"
  Group = -> [Dimension027,Dimension028,Dimension029,Dimension030,Dimension031,Dimension032,Dimension033,Dimension034,Dimension035,Dimension036,Dimension037,Dimension038,Dimension039,Dimension040]
FEATURE [App::DocumentObjectGroup] Group009  label="Plan 2"
  Group = -> [mirror439,mirror440,mirror441,mirror442,mirror443,Compound094,DWire024,mirror449,mirror450,mirror452,mirror453,Rectangle224,Compound095,Rectangle225,Rectangle229,mirror464,mirror466,DWire025,DWire026,mirror467,mirror468,mirror469,mirror479,mirror480,mirror481,mirror454,mirror482,mirror483,mirror484,Rectangle242,Group013]
FEATURE [App::Annotation] Text003  label="Option 2"
  LabelText = OPTION 2
  Position = (33174.9,216.757,0)
FEATURE [App::Annotation] Text004  label="Option 1"
  LabelText = OPTION 1
  Position = (17544,216.757,0)
FEATURE [App::Annotation] Text005  label="BATH"
  LabelText = BATH
  Position = (17680,5204.54,0)
FEATURE [App::Annotation] Text006  label="BATH001"
  LabelText = BATH
  Position = (33371,3946.24,0)
FEATURE [App::Annotation] Text007
  LabelText = KITCHEN
  Position = (20130.8,7126.87,0)
FEATURE [App::Annotation] Text008
  LabelText = LIVING
  Position = (23497,5480.93,0)
FEATURE [App::Annotation] Text009
  LabelText = BEDROOM
  Position = (25997.6,3478.64,0)
FEATURE [App::Annotation] Text010
  LabelText = BEDROOM
  Position = (38137.2,3259.31,0)
FEATURE [App::Annotation] Text011
  LabelText = LIVING
  Position = (37872.7,8319.72,0)
FEATURE [App::Annotation] Text012
  LabelText = KITCHEN
  Position = (33954,8880.69,0)
FEATURE [Part::Part2DObjectPython] DWire027  # Draft 2D object (typed FeaturePython)
  ChamferSize = 0
  Closed = true
  End = (25716.3,3816.15,0)
  FilletRadius = 0
  Length = 70465.9
  MakeFace = true
  Points = (37) [(24488,3816.15,0),(24488,3969.69,0),(25869.9,3969.69,0),(25869.9,3369.69,0),(28868.1,3369.69,0),(28868.1,7369.69,0),(25869.9,7369.69,0),+30 more]
  Start = (24488,3816.15,0)
  Subdivisions = 0
FEATURE [App::FeaturePython] Dimension041  # Draft dimension (typed FeaturePython)
  Diameter = false
  Dimline = (35177.9,6107.7,0)
  Direction = (0,0,0)
  Distance = 1908.56
  End = (35037.1,4199.14,0)
  Normal = (0,0,1)
  Start = (35037.1,6107.7,0)
